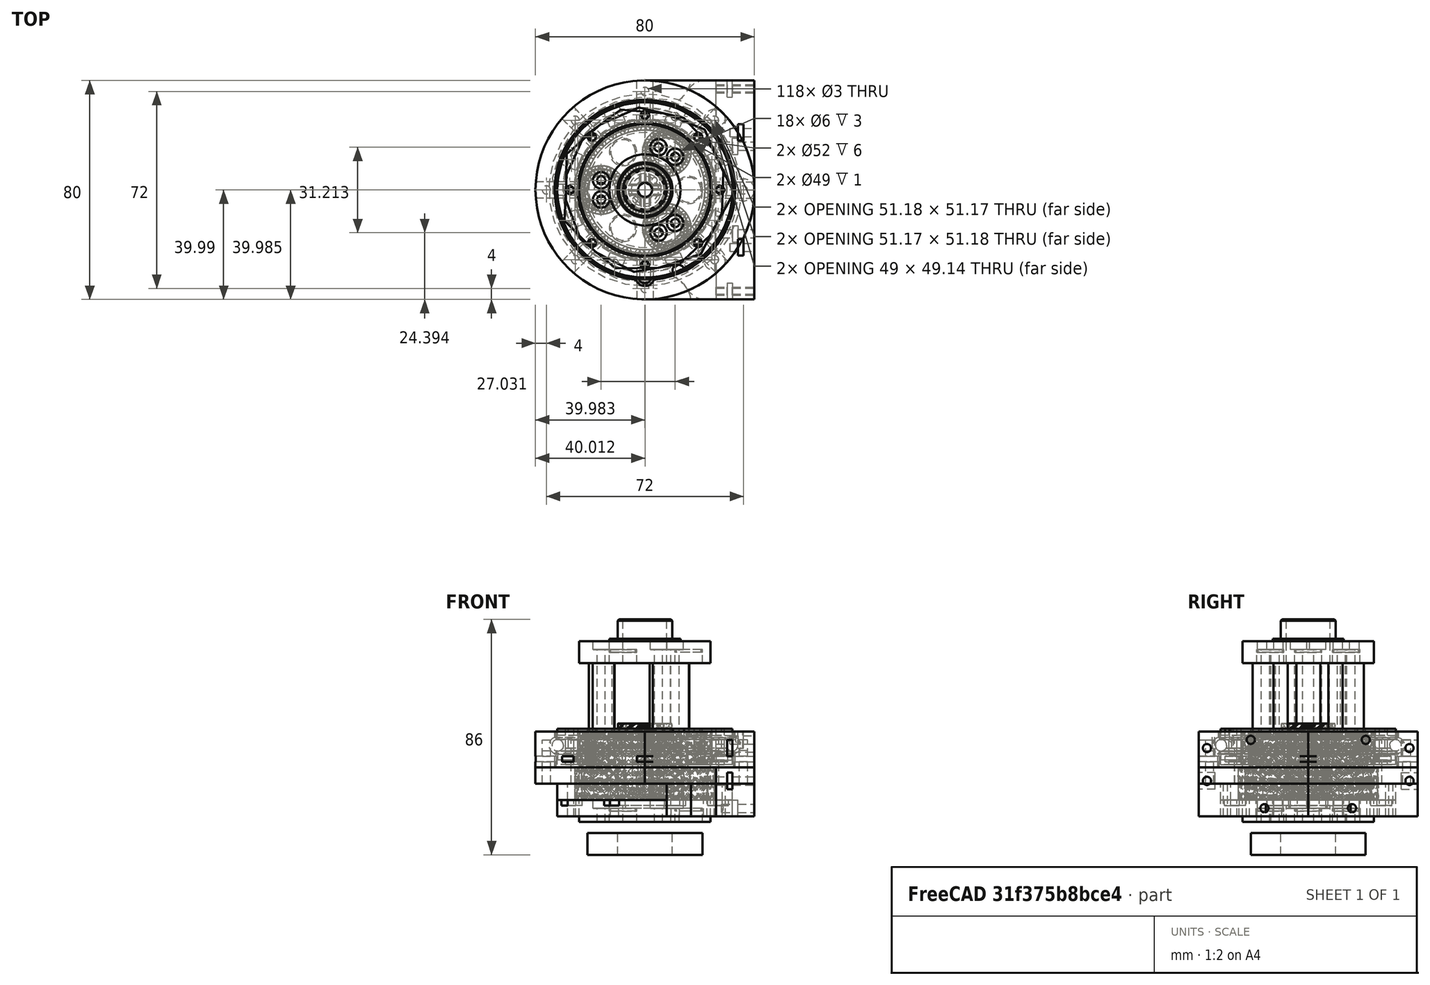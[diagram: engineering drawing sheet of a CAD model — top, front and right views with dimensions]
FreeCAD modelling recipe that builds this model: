
FCSTD DOCUMENT  (FreeCAD 0.19R24276 (Git))
Label: J-mini_024
License: All rights reserved
LicenseURL: http://en.wikipedia.org/wiki/All_rights_reserved
objects: Part::Cylinder×259, Part::Cut×154, Part::Box×112, Part::Compound×108, Part::FeaturePython×40, Mesh::Feature×18, Part::Chamfer×7, Part::Torus×6, Part::Mirroring×2, Part::Fillet×1
note: 689 computed .brp shape members not serialized (recipe doc carries the construction recipe); baked Part::Feature solids carry a one-line shape summary decoded from their .brp

FEATURE [Part::Cylinder] Cylinder190  label="Válec190"
  Angle = 360
  AttacherType = Attacher::AttachEngine3D
  Height = 20
  Placement = pos=(25.4558,-25.4558,0) rot=(0,0,-1;0.785398rad)
  Radius = 1.5
FEATURE [Part::Cylinder] Cylinder188  label="Válec188"
  Angle = 360
  AttacherType = Attacher::AttachEngine3D
  Height = 6
  Radius = 32
FEATURE [Part::Cylinder] Cylinder189  label="Válec189"
  Angle = 360
  AttacherType = Attacher::AttachEngine3D
  Height = 6
  Radius = 40
FEATURE [Part::Cylinder] Cylinder193  label="Válec193"
  Angle = 360
  AttacherType = Attacher::AttachEngine3D
  Height = 20
  Placement = pos=(25.4558,25.4558,0) rot=(0,0,1;0.785398rad)
  Radius = 1.5
FEATURE [Part::Cylinder] Cylinder196  label="Válec196"
  Angle = 360
  AttacherType = Attacher::AttachEngine3D
  Height = 20
  Placement = pos=(1.2e-14,-36,0) rot=(0,0,-1;1.5708rad)
  Radius = 1.5
FEATURE [Part::Cylinder] Cylinder194  label="Válec194"
  Angle = 360
  AttacherType = Attacher::AttachEngine3D
  Height = 20
  Placement = pos=(36,0,0) rot=(0,0,1;0rad)
  Radius = 1.5
FEATURE [Part::Cylinder] Cylinder191  label="Válec191"
  Angle = 360
  AttacherType = Attacher::AttachEngine3D
  Height = 20
  Placement = pos=(-25.4558,-25.4558,0) rot=(0,0,1;3.92699rad)
  Radius = 1.5
FEATURE [Part::Box] Box055  label="Krychle055"
  AttacherType = Attacher::AttachEngine3D
  Height = 2
  Length = 6
  Placement = pos=(22.8728,-12.7214,-2) rot=(0,0,-1;0.392699rad)
  Width = 6
FEATURE [Part::Cylinder] Cylinder198  label="Válec198"
  Angle = 360
  AttacherType = Attacher::AttachEngine3D
  Height = 20
  Placement = pos=(11.0978,-26.7925,-10) rot=(0,0,-1;1.1781rad)
  Radius = 1.5
FEATURE [Part::Box] Box057  label="Krychle057"
  AttacherType = Attacher::AttachEngine3D
  Height = 6
  Length = 2
  Placement = pos=(30,34,4) rot=(0,0,1;0rad)
  Width = 6
FEATURE [Part::Box] Box058  label="Krychle058"
  AttacherType = Attacher::AttachEngine3D
  Height = 2
  Length = 6
  Placement = pos=(12.7214,22.8728,-2) rot=(0,0,1;1.1781rad)
  Width = 6
FEATURE [Part::Box] Box059  label="Krychle059"
  AttacherType = Attacher::AttachEngine3D
  Height = 2
  Length = 6
  Placement = pos=(-25.1689,-7.17813,-2) rot=(0,0,1;3.53429rad)
  Width = 6
FEATURE [Part::Cylinder] Cylinder195  label="Válec195"
  Angle = 360
  AttacherType = Attacher::AttachEngine3D
  Height = 20
  Placement = pos=(-4e-15,36,0) rot=(0,0,1;1.5708rad)
  Radius = 1.5
FEATURE [Part::Box] Box056  label="Krychle056"
  AttacherType = Attacher::AttachEngine3D
  Height = 2
  Length = 6
  Placement = pos=(-7.17813,25.1689,-2) rot=(0,0,1;1.96349rad)
  Width = 6
FEATURE [Part::Cylinder] Cylinder197  label="Válec197"
  Angle = 360
  AttacherType = Attacher::AttachEngine3D
  Height = 20
  Placement = pos=(-36,-1.1e-14,0) rot=(0,0,1;3.14159rad)
  Radius = 1.5
FEATURE [Part::Cylinder] Cylinder199  label="Válec199"
  Angle = 360
  AttacherType = Attacher::AttachEngine3D
  Height = 20
  Placement = pos=(26.7925,11.0978,-10) rot=(0,0,1;0.392699rad)
  Radius = 1.5
FEATURE [Part::Box] Box060  label="Krychle060"
  AttacherType = Attacher::AttachEngine3D
  Height = 2
  Length = 6
  Placement = pos=(-22.8728,12.7214,-2) rot=(0,0,1;2.74889rad)
  Width = 6
FEATURE [Part::Box] Box061  label="Krychle061"
  AttacherType = Attacher::AttachEngine3D
  Height = 2
  Length = 6
  Placement = pos=(25.1689,7.17813,-2) rot=(0,0,1;0.392699rad)
  Width = 6
FEATURE [Part::Cylinder] Cylinder192  label="Válec192"
  Angle = 360
  AttacherType = Attacher::AttachEngine3D
  Height = 20
  Placement = pos=(-25.4558,25.4558,0) rot=(0,0,1;2.35619rad)
  Radius = 1.5
FEATURE [Part::FeaturePython] wormgear032  # WARN: FeaturePython — macro-defined, semantics opaque (R4)
  AttacherType = Attacher::AttachEngine3D
  Placement = pos=(0,0,0) rot=(0,0,1;0.011345rad)
  beta = 36.5317
  clearance = 0.25
  diameter = 49
  head = 0
  height = 20
  module = 1.1
  pressure_angle = 20
  reverse_pitch = true
  teeth = 33
  version = 0.0.3
FEATURE [Part::Cut] Cut142
  Base = -> Cylinder189
  Placement = pos=(0,0,6) rot=(0,0,-1;0.017453rad)
  Tool = -> wormgear032
FEATURE [Part::FeaturePython] wormgear033  # WARN: FeaturePython — macro-defined, semantics opaque (R4)
  AttacherType = Attacher::AttachEngine3D
  Placement = pos=(0,0,0) rot=(0,0,1;0.043633rad)
  beta = 36.5317
  clearance = 0.25
  diameter = 49
  head = 0
  height = 20
  module = 1.1
  pressure_angle = 20
  reverse_pitch = false
  teeth = 33
  version = 0.0.3
FEATURE [Part::Cut] Cut141
  Base = -> Cylinder188
  Tool = -> wormgear033
FEATURE [Part::FeaturePython] Tube010  # WARN: FeaturePython — macro-defined, semantics opaque (R4)
  AttacherType = Attacher::AttachEngine3D
  Height = 6
  InnerRadius = 26
  OuterRadius = 32
  Placement = pos=(0,0,-6) rot=(0,0,1;0rad)
FEATURE [Part::Compound] Compound127
  Links = -> [Cylinder190,Cylinder194,Cylinder193,Cylinder195,Cylinder192,Cylinder197,Cylinder191,Cylinder196]
FEATURE [Part::Cut] Cut144
  Base = -> Cut142
  Tool = -> Compound127
FEATURE [Part::Box] Box064  label="Krychle064"
  AttacherType = Attacher::AttachEngine3D
  Height = 6
  Length = 40
  Placement = pos=(0,0,6) rot=(0,0,1;0rad)
  Width = 40
FEATURE [Part::Cylinder] Cylinder205  label="Válec205"
  Angle = 360
  AttacherType = Attacher::AttachEngine3D
  Height = 20
  Placement = pos=(26.7925,-11.0978,-10) rot=(0,0,-1;0.392699rad)
  Radius = 1.5
FEATURE [Part::Cylinder] Cylinder204  label="Válec204"
  Angle = 360
  AttacherType = Attacher::AttachEngine3D
  Height = 20
  Placement = pos=(-26.7925,11.0978,-10) rot=(0,0,1;2.74889rad)
  Radius = 1.5
FEATURE [Part::Box] Box065  label="Krychle065"
  AttacherType = Attacher::AttachEngine3D
  Height = 6
  Length = 2
  Placement = pos=(30,34,4) rot=(0,0,1;0rad)
  Width = 6
FEATURE [Part::Cylinder] Cylinder209  label="Válec209"
  Angle = 360
  AttacherType = Attacher::AttachEngine3D
  Height = 20
  Placement = pos=(25.4558,25.4558,0) rot=(0,0,1;0.785398rad)
  Radius = 1.5
FEATURE [Part::Cylinder] Cylinder208  label="Válec208"
  Angle = 360
  AttacherType = Attacher::AttachEngine3D
  Height = 20
  Placement = pos=(36,0,0) rot=(0,0,1;0rad)
  Radius = 1.5
FEATURE [Part::Cylinder] Cylinder201  label="Válec201"
  Angle = 360
  AttacherType = Attacher::AttachEngine3D
  Height = 20
  Placement = pos=(-11.0978,26.7925,-10) rot=(0,0,1;1.96349rad)
  Radius = 1.5
FEATURE [Part::Box] Box066  label="Krychle066"
  AttacherType = Attacher::AttachEngine3D
  Height = 18
  Length = 14
  Placement = pos=(26,0,-6) rot=(0,0,1;0rad)
  Width = 40
FEATURE [Part::Cylinder] Cylinder200  label="Válec200"
  Angle = 360
  AttacherType = Attacher::AttachEngine3D
  Height = 20
  Placement = pos=(11.0978,26.7925,-10) rot=(0,0,1;1.1781rad)
  Radius = 1.5
FEATURE [Part::Cylinder] Cylinder210  label="Válec210"
  Angle = 360
  AttacherType = Attacher::AttachEngine3D
  Height = 30
  Placement = pos=(36,0,-24) rot=(0,0,1;0rad)
  Radius = 4
FEATURE [Part::Box] Box062  label="Krychle062"
  AttacherType = Attacher::AttachEngine3D
  Height = 2
  Length = 6
  Placement = pos=(-12.7214,-22.8728,-2) rot=(0,0,-1;1.96349rad)
  Width = 6
FEATURE [Part::Cylinder] Cylinder202  label="Válec202"
  Angle = 360
  AttacherType = Attacher::AttachEngine3D
  Height = 20
  Placement = pos=(-26.7925,-11.0978,-10) rot=(0,0,1;3.53429rad)
  Radius = 1.5
FEATURE [Part::Cylinder] Cylinder203  label="Válec203"
  Angle = 360
  AttacherType = Attacher::AttachEngine3D
  Height = 20
  Placement = pos=(-11.0978,-26.7925,-10) rot=(0,0,-1;1.96349rad)
  Radius = 1.5
FEATURE [Part::Compound] Compound125
  Links = -> [Cylinder199,Cylinder200,Cylinder201,Cylinder204,Cylinder202,Cylinder203,Cylinder198,Cylinder205]
FEATURE [Part::Box] Box063  label="Krychle063"
  AttacherType = Attacher::AttachEngine3D
  Height = 2
  Length = 6
  Placement = pos=(7.17813,-25.1689,-2) rot=(0,0,-1;1.1781rad)
  Width = 6
FEATURE [Part::Compound] Compound126
  Links = -> [Box061,Box058,Box056,Box060,Box059,Box062,Box063,Box055]
FEATURE [Part::Cylinder] Cylinder206  label="Válec206"
  Angle = 360
  AttacherType = Attacher::AttachEngine3D
  Height = 20
  Placement = pos=(26,37,7) rot=(0,1,0;1.5708rad)
  Radius = 1.5
FEATURE [Part::Cylinder] Cylinder207  label="Válec207"
  Angle = 360
  AttacherType = Attacher::AttachEngine3D
  Height = 6
  Placement = pos=(0,0,6) rot=(0,0,1;0rad)
  Radius = 40
FEATURE [Part::Cut] Cut138
  Base = -> Box064
  Tool = -> Cylinder207
FEATURE [Part::Cut] Cut135
  Base = -> Cut138
  Tool = -> Box057
FEATURE [Part::Cut] Cut134
  Base = -> Cut135
  Tool = -> Cylinder206
FEATURE [Part::Cut] Cut151
  Base = -> Tube010
  Tool = -> Compound126
FEATURE [Part::Cut] Cut136
  Base = -> Cut151
  Tool = -> Compound125
FEATURE [Part::Cylinder] Cylinder212  label="Válec212"
  Angle = 360
  AttacherType = Attacher::AttachEngine3D
  Height = 20
  Placement = pos=(26,37,7) rot=(0,1,0;1.5708rad)
  Radius = 1.5
FEATURE [Part::Cylinder] Cylinder220  label="Válec220"
  Angle = 360
  AttacherType = Attacher::AttachEngine3D
  Height = 30
  Placement = pos=(25.4558,25.4558,-24) rot=(0,0,1;0.785398rad)
  Radius = 4
FEATURE [Part::Cylinder] Cylinder214  label="Válec214"
  Angle = 360
  AttacherType = Attacher::AttachEngine3D
  Height = 20
  Placement = pos=(28,16,-3) rot=(0,1,0;1.5708rad)
  Radius = 1.5
FEATURE [Part::Compound] Compound132
  Links = -> [Cylinder214,Cylinder212]
FEATURE [Part::Cylinder] Cylinder217  label="Válec217"
  Angle = 360
  AttacherType = Attacher::AttachEngine3D
  Height = 12
  Placement = pos=(0,0,-6) rot=(0,0,1;0rad)
  Radius = 32
FEATURE [Part::Cylinder] Cylinder221  label="Válec221"
  Angle = 360
  AttacherType = Attacher::AttachEngine3D
  Height = 6
  Placement = pos=(0,0,6) rot=(0,0,1;0rad)
  Radius = 40
FEATURE [Part::Box] Box068  label="Krychle068"
  AttacherType = Attacher::AttachEngine3D
  Height = 6
  Length = 2
  Placement = pos=(30,34,4) rot=(0,0,1;0rad)
  Width = 6
FEATURE [Part::Box] Box070  label="Krychle070"
  AttacherType = Attacher::AttachEngine3D
  Height = 12
  Length = 18
  Placement = pos=(8,10,-6) rot=(0,0,1;0rad)
  Width = 30
FEATURE [Part::Box] Box071  label="Krychle071"
  AttacherType = Attacher::AttachEngine3D
  Height = 6
  Length = 40
  Placement = pos=(0,0,6) rot=(0,0,1;0rad)
  Width = 40
FEATURE [Part::Cut] Cut152
  Base = -> Box071
  Tool = -> Cylinder221
FEATURE [Part::Box] Box067  label="Krychle067"
  AttacherType = Attacher::AttachEngine3D
  Height = 6
  Length = 2
  Placement = pos=(32,13,-6) rot=(0,0,1;0rad)
  Width = 6
FEATURE [Part::Compound] Compound131
  Links = -> [Box067,Box065]
FEATURE [Part::Cylinder] Cylinder218  label="Válec218"
  Angle = 360
  AttacherType = Attacher::AttachEngine3D
  Height = 12
  Placement = pos=(0,0,-6) rot=(0,0,1;0rad)
  Radius = 32
FEATURE [Part::Cylinder] Cylinder219  label="Válec219"
  Angle = 360
  AttacherType = Attacher::AttachEngine3D
  Height = 12
  Placement = pos=(6,41.8,-6) rot=(0,0,1;0rad)
  Radius = 11
FEATURE [Part::Cut] Cut148
  Base = -> Box070
  Tool = -> Cylinder219
FEATURE [Part::Cut] Cut147
  Base = -> Cut148
  Tool = -> Cylinder218
FEATURE [Part::Cut] Cut149
  Base = -> Cut147
  Tool = -> Cylinder220
FEATURE [Part::Cylinder] Cylinder215  label="Válec215"
  Angle = 360
  AttacherType = Attacher::AttachEngine3D
  Height = 20
  Placement = pos=(26,37,7) rot=(0,1,0;1.5708rad)
  Radius = 1.5
FEATURE [Part::Box] Box069  label="Krychle069"
  AttacherType = Attacher::AttachEngine3D
  Height = 6
  Length = 2
  Placement = pos=(30,34,4) rot=(0,0,1;0rad)
  Width = 6
FEATURE [Part::Cut] Cut150
  Base = -> Cut152
  Tool = -> Box069
FEATURE [Part::Cut] Cut143
  Base = -> Cut150
  Tool = -> Cylinder215
FEATURE [Part::Cylinder] Cylinder213  label="Válec213"
  Angle = 360
  AttacherType = Attacher::AttachEngine3D
  Height = 30
  Placement = pos=(25.4558,25.4558,-24) rot=(0,0,1;0.785398rad)
  Radius = 4
FEATURE [Part::Cylinder] Cylinder216  label="Válec216"
  Angle = 360
  AttacherType = Attacher::AttachEngine3D
  Height = 20
  Placement = pos=(36,0,0) rot=(0,0,1;0rad)
  Radius = 1.5
FEATURE [Part::Cylinder] Cylinder211  label="Válec211"
  Angle = 360
  AttacherType = Attacher::AttachEngine3D
  Height = 12
  Placement = pos=(0,0,-6) rot=(0,0,1;0rad)
  Radius = 32
FEATURE [Part::Cut] Cut162
  Base = -> Box066
  Tool = -> Cylinder211
FEATURE [Part::Cut] Cut137
  Base = -> Cut162
  Tool = -> Cylinder210
FEATURE [Part::Cut] Cut140
  Base = -> Cut137
  Tool = -> Cylinder208
FEATURE [Part::Cut] Cut163
  Base = -> Cut140
  Tool = -> Cylinder213
FEATURE [Part::Cut] Cut146
  Base = -> Cut163
  Tool = -> Cylinder209
FEATURE [Part::Cut] Cut164
  Base = -> Cut146
  Tool = -> Compound132
FEATURE [Part::Cut] Cut145
  Base = -> Cut164
  Tool = -> Compound131
FEATURE [Part::Compound] Compound133
  Links = -> [Cut145,Cut149,Cut134]
FEATURE [Part::Cylinder] Cylinder223  label="Válec223"
  Angle = 360
  AttacherType = Attacher::AttachEngine3D
  Height = 30
  Placement = pos=(36,0,-24) rot=(0,0,1;0rad)
  Radius = 4
FEATURE [Part::Cylinder] Cylinder225  label="Válec225"
  Angle = 360
  AttacherType = Attacher::AttachEngine3D
  Height = 12
  Placement = pos=(0,0,-6) rot=(0,0,1;0rad)
  Radius = 32
FEATURE [Part::Cylinder] Cylinder222  label="Válec222"
  Angle = 360
  AttacherType = Attacher::AttachEngine3D
  Height = 20
  Placement = pos=(25.4558,25.4558,0) rot=(0,0,1;0.785398rad)
  Radius = 1.5
FEATURE [Part::Cylinder] Cylinder226  label="Válec226"
  Angle = 360
  AttacherType = Attacher::AttachEngine3D
  Height = 20
  Placement = pos=(26,37,7) rot=(0,1,0;1.5708rad)
  Radius = 1.5
FEATURE [Part::Cylinder] Cylinder227  label="Válec227"
  Angle = 360
  AttacherType = Attacher::AttachEngine3D
  Height = 12
  Placement = pos=(6,41.8,-6) rot=(0,0,1;0rad)
  Radius = 11
FEATURE [Part::Cylinder] Cylinder228  label="Válec228"
  Angle = 360
  AttacherType = Attacher::AttachEngine3D
  Height = 30
  Placement = pos=(25.4558,25.4558,-24) rot=(0,0,1;0.785398rad)
  Radius = 4
FEATURE [Part::Cylinder] Cylinder229  label="Válec229"
  Angle = 360
  AttacherType = Attacher::AttachEngine3D
  Height = 20
  Placement = pos=(28,16,-3) rot=(0,1,0;1.5708rad)
  Radius = 1.5
FEATURE [Part::Compound] Compound130
  Links = -> [Cylinder229,Cylinder226]
FEATURE [Part::Box] Box073  label="Krychle073"
  AttacherType = Attacher::AttachEngine3D
  Height = 12
  Length = 18
  Placement = pos=(8,10,-6) rot=(0,0,1;0rad)
  Width = 30
FEATURE [Part::Cut] Cut155
  Base = -> Box073
  Tool = -> Cylinder227
FEATURE [Part::Cut] Cut158
  Base = -> Cut155
  Tool = -> Cylinder225
FEATURE [Part::Cut] Cut156
  Base = -> Cut158
  Tool = -> Cylinder228
FEATURE [Part::Cylinder] Cylinder224  label="Válec224"
  Angle = 360
  AttacherType = Attacher::AttachEngine3D
  Height = 30
  Placement = pos=(25.4558,25.4558,-24) rot=(0,0,1;0.785398rad)
  Radius = 4
FEATURE [Part::Box] Box072  label="Krychle072"
  AttacherType = Attacher::AttachEngine3D
  Height = 18
  Length = 14
  Placement = pos=(26,0,-6) rot=(0,0,1;0rad)
  Width = 40
FEATURE [Part::Cut] Cut160
  Base = -> Box072
  Tool = -> Cylinder217
FEATURE [Part::Cut] Cut139
  Base = -> Cut160
  Tool = -> Cylinder223
FEATURE [Part::Cut] Cut161
  Base = -> Cut139
  Tool = -> Cylinder216
FEATURE [Part::Cut] Cut157
  Base = -> Cut161
  Tool = -> Cylinder224
FEATURE [Part::Cut] Cut153
  Base = -> Cut157
  Tool = -> Cylinder222
FEATURE [Part::Cut] Cut159
  Base = -> Cut153
  Tool = -> Compound130
FEATURE [Part::Box] Box074  label="Krychle074"
  AttacherType = Attacher::AttachEngine3D
  Height = 6
  Length = 2
  Placement = pos=(32,13,-6) rot=(0,0,1;0rad)
  Width = 6
FEATURE [Part::Compound] Compound128
  Links = -> [Box074,Box068]
FEATURE [Part::Cut] Cut154
  Base = -> Cut159
  Tool = -> Compound128
FEATURE [Part::Compound] Compound129
  Links = -> [Cut154,Cut156,Cut143]
FEATURE [Part::Mirroring] mirror001  label="Compound123 (mirrored)001"
  Base = (1,0,0)
  Normal = (1e-16,-1,0)
  Source = -> Compound129
FEATURE [Part::Compound] Compound134  label="jointovina_micro_monoblok_hrubo001"
  Links = -> [Compound133,mirror001,Cut136,Cut141,Cut144]
FEATURE [Part::Fillet] Fillet  label="J-mini_monoblock_old"
  Base = -> Compound134
  Edges = 2 edges r=8: [Edge90,Edge230]
FEATURE [Part::Torus] Torus006  label="Anuloid006"
  Angle1 = -180
  Angle2 = 180
  Angle3 = 360
  AttacherType = Attacher::AttachEngine3D
  Placement = pos=(0,0,20) rot=(0,0,1;0rad)
  Radius1 = 32
  Radius2 = 2.2
FEATURE [Part::Torus] Torus005  label="Anuloid005"
  Angle1 = -180
  Angle2 = 180
  Angle3 = 360
  AttacherType = Attacher::AttachEngine3D
  Placement = pos=(0,0,20) rot=(0,0,1;0rad)
  Radius1 = 32
  Radius2 = 2.2
FEATURE [Part::FeaturePython] wormgear043  # WARN: FeaturePython — macro-defined, semantics opaque (R4)
  AttacherType = Attacher::AttachEngine3D
  Placement = pos=(0,0,12) rot=(0,0,1;0.169297rad)
  beta = 35.3625
  clearance = 0.25
  diameter = 46.5
  head = 0.2
  height = 8
  module = 1.1
  pressure_angle = 20
  reverse_pitch = false
  teeth = 30
  version = 0.0.3
FEATURE [Part::FeaturePython] Tube051  # WARN: FeaturePython — macro-defined, semantics opaque (R4)
  AttacherType = Attacher::AttachEngine3D
  Height = 1
  InnerRadius = 24.5
  OuterRadius = 32
  Placement = pos=(0,0,25) rot=(0,0,1;0rad)
FEATURE [Part::FeaturePython] wormgear042  # WARN: FeaturePython — macro-defined, semantics opaque (R4)
  AttacherType = Attacher::AttachEngine3D
  Placement = pos=(0,0,18) rot=(0,0,-1;0.18326rad)
  beta = 35.3625
  clearance = 0.25
  diameter = 46.5
  head = 0.2
  height = 8
  module = 1.1
  pressure_angle = 20
  reverse_pitch = true
  teeth = 30
  version = 0.0.3
FEATURE [Part::Cylinder] Cylinder1256  label="Válec1256"
  Angle = 360
  AttacherType = Attacher::AttachEngine3D
  Height = 20
  Placement = pos=(1.1e-14,-27,19) rot=(0,0,1;3.14159rad)
  Radius = 1
FEATURE [Part::Box] Box403  label="Krychle403"
  AttacherType = Attacher::AttachEngine3D
  Height = 1.4
  Length = 4
  Placement = pos=(18.74,-15.91,23.6) rot=(0,0,1;3.92699rad)
  Width = 8
FEATURE [Part::Cylinder] Cylinder1250  label="Válec1250"
  Angle = 360
  AttacherType = Attacher::AttachEngine3D
  Height = 20
  Placement = pos=(-19.0919,19.0919,19) rot=(0,0,1;0.785398rad)
  Radius = 1
FEATURE [Part::Cylinder] Cylinder1254  label="Válec1254"
  Angle = 360
  AttacherType = Attacher::AttachEngine3D
  Height = 20
  Placement = pos=(-27,-4e-15,19) rot=(0,0,1;1.5708rad)
  Radius = 1
FEATURE [Part::Cylinder] Cylinder1253  label="Válec1253"
  Angle = 360
  AttacherType = Attacher::AttachEngine3D
  Height = 6
  Placement = pos=(0,0,13) rot=(0,0,1;0rad)
  Radius = 32
FEATURE [Part::Cut] Cut471
  Base = -> Cylinder1253
  Tool = -> wormgear043
FEATURE [Part::Cylinder] Cylinder1261  label="Válec1261"
  Angle = 360
  AttacherType = Attacher::AttachEngine3D
  Height = 20
  Placement = pos=(19.0919,-19.0919,19) rot=(0,0,1;3.92699rad)
  Radius = 1
FEATURE [Part::Cylinder] Cylinder1255  label="Válec1255"
  Angle = 360
  AttacherType = Attacher::AttachEngine3D
  Height = 20
  Placement = pos=(0,27,19) rot=(0,0,1;0rad)
  Radius = 1
FEATURE [Part::Box] Box404  label="Krychle404"
  AttacherType = Attacher::AttachEngine3D
  Height = 1.4
  Length = 4
  Placement = pos=(-15.91,-18.74,23.6) rot=(0,0,1;2.35619rad)
  Width = 8
FEATURE [Part::Cylinder] Cylinder1257  label="Válec1257"
  Angle = 360
  AttacherType = Attacher::AttachEngine3D
  Height = 20
  Placement = pos=(1.1e-14,-27,19) rot=(0,0,1;3.14159rad)
  Radius = 1
FEATURE [Part::Cylinder] Cylinder1266  label="Válec1266"
  Angle = 360
  AttacherType = Attacher::AttachEngine3D
  Height = 20
  Placement = pos=(-27,-4e-15,19) rot=(0,0,1;1.5708rad)
  Radius = 1
FEATURE [Part::Box] Box402  label="Krychle402"
  AttacherType = Attacher::AttachEngine3D
  Height = 1.4
  Length = 4
  Placement = pos=(-2,24.5,23.6) rot=(0,0,1;0rad)
  Width = 8
FEATURE [Part::Cylinder] Cylinder1252  label="Válec1252"
  Angle = 360
  AttacherType = Attacher::AttachEngine3D
  Height = 6
  Placement = pos=(0,0,19) rot=(0,0,1;0rad)
  Radius = 32
FEATURE [Part::Cut] Cut472
  Base = -> Cylinder1252
  Tool = -> wormgear042
FEATURE [Part::Cylinder] Cylinder1251  label="Válec1251"
  Angle = 360
  AttacherType = Attacher::AttachEngine3D
  Height = 20
  Placement = pos=(0,27,19) rot=(0,0,1;0rad)
  Radius = 1
FEATURE [Part::Box] Box406  label="Krychle406"
  AttacherType = Attacher::AttachEngine3D
  Height = 1.4
  Length = 4
  Placement = pos=(-24.5,-2,23.6) rot=(0,0,1;1.5708rad)
  Width = 8
FEATURE [Part::Cylinder] Cylinder1262  label="Válec1262"
  Angle = 360
  AttacherType = Attacher::AttachEngine3D
  Height = 10
  Placement = pos=(12.2459,-29.5641,20) rot=(0,0,1;0.392699rad)
  Radius = 2.2
FEATURE [Part::Cylinder] Cylinder1259  label="Válec1259"
  Angle = 360
  AttacherType = Attacher::AttachEngine3D
  Height = 20
  Placement = pos=(27,1e-14,19) rot=(0,0,-1;1.5708rad)
  Radius = 1
FEATURE [Part::Cylinder] Cylinder1260  label="Válec1260"
  Angle = 360
  AttacherType = Attacher::AttachEngine3D
  Height = 20
  Placement = pos=(19.0919,19.0919,19) rot=(0,0,-1;0.785398rad)
  Radius = 1
FEATURE [Part::Cylinder] Cylinder1258  label="Válec1258"
  Angle = 360
  AttacherType = Attacher::AttachEngine3D
  Height = 20
  Placement = pos=(-19.0919,-19.0919,19) rot=(0,0,1;2.35619rad)
  Radius = 1
FEATURE [Part::Compound] Compound681
  Links = -> [Cylinder1251,Cylinder1250,Cylinder1254,Cylinder1258,Cylinder1257,Cylinder1261,Cylinder1259,Cylinder1260]
FEATURE [Part::Box] Box408  label="Krychle408"
  AttacherType = Attacher::AttachEngine3D
  Height = 1.4
  Length = 4
  Placement = pos=(2,-24.5,23.6) rot=(0,0,1;3.14159rad)
  Width = 8
FEATURE [Part::Box] Box405  label="Krychle405"
  AttacherType = Attacher::AttachEngine3D
  Height = 1.4
  Length = 4
  Placement = pos=(-18.74,15.91,23.6) rot=(0,0,1;0.785398rad)
  Width = 8
FEATURE [Part::Box] Box409  label="Krychle409"
  AttacherType = Attacher::AttachEngine3D
  Height = 1.4
  Length = 4
  Placement = pos=(15.91,18.74,23.6) rot=(0,0,-1;0.785398rad)
  Width = 8
FEATURE [Part::Cylinder] Cylinder1263  label="Válec1263"
  Angle = 360
  AttacherType = Attacher::AttachEngine3D
  Height = 20
  Placement = pos=(-19.0919,19.0919,19) rot=(0,0,1;0.785398rad)
  Radius = 1
FEATURE [Part::Cylinder] Cylinder1264  label="Válec1264"
  Angle = 360
  AttacherType = Attacher::AttachEngine3D
  Height = 20
  Placement = pos=(-27,-4e-15,19) rot=(0,0,1;1.5708rad)
  Radius = 1
FEATURE [Part::Box] Box407  label="Krychle407"
  AttacherType = Attacher::AttachEngine3D
  Height = 1.4
  Length = 4
  Placement = pos=(24.5,2,23.6) rot=(0,0,-1;1.5708rad)
  Width = 8
FEATURE [Part::Compound] Compound678
  Links = -> [Box402,Box405,Box406,Box404,Box408,Box403,Box407,Box409]
FEATURE [Part::Cut] Cut474
  Base = -> Cut472
  Tool = -> Compound678
FEATURE [Part::Cut] Cut475
  Base = -> Cut474
  Tool = -> Compound681
FEATURE [Part::Cut] Cut478
  Base = -> Cut475
  Tool = -> Torus006
FEATURE [Part::Cut] Cut480
  Base = -> Cut478
  Tool = -> Cylinder1262
FEATURE [Part::Cylinder] Cylinder1265  label="Válec1265"
  Angle = 360
  AttacherType = Attacher::AttachEngine3D
  Height = 20
  Placement = pos=(-19.0919,-19.0919,19) rot=(0,0,1;2.35619rad)
  Radius = 1
FEATURE [Part::Cylinder] Cylinder1276  label="Válec1276"
  Angle = 360
  AttacherType = Attacher::AttachEngine3D
  Height = 20
  Placement = pos=(0,27,19) rot=(0,0,1;0rad)
  Radius = 1
FEATURE [Part::Cylinder] Cylinder1277  label="Válec1277"
  Angle = 360
  AttacherType = Attacher::AttachEngine3D
  Height = 20
  Placement = pos=(-19.0919,-19.0919,19) rot=(0,0,1;2.35619rad)
  Radius = 1
FEATURE [Part::Cylinder] Cylinder1272  label="Válec1272"
  Angle = 360
  AttacherType = Attacher::AttachEngine3D
  Height = 20
  Placement = pos=(-19.0919,19.0919,19) rot=(0,0,1;0.785398rad)
  Radius = 1
FEATURE [Part::Cylinder] Cylinder1271  label="Válec1271"
  Angle = 360
  AttacherType = Attacher::AttachEngine3D
  Height = 20
  Placement = pos=(27,1e-14,19) rot=(0,0,-1;1.5708rad)
  Radius = 1
FEATURE [Part::Cylinder] Cylinder1269  label="Válec1269"
  Angle = 360
  AttacherType = Attacher::AttachEngine3D
  Height = 20
  Placement = pos=(1.1e-14,-27,19) rot=(0,0,1;3.14159rad)
  Radius = 1
FEATURE [Part::Cylinder] Cylinder1274  label="Válec1274"
  Angle = 360
  AttacherType = Attacher::AttachEngine3D
  Height = 20
  Placement = pos=(27,1e-14,19) rot=(0,0,-1;1.5708rad)
  Radius = 1
FEATURE [Part::Cylinder] Cylinder1268  label="Válec1268"
  Angle = 360
  AttacherType = Attacher::AttachEngine3D
  Height = 20
  Placement = pos=(19.0919,-19.0919,19) rot=(0,0,1;3.92699rad)
  Radius = 1
FEATURE [Part::Cylinder] Cylinder1267  label="Válec1267"
  Angle = 360
  AttacherType = Attacher::AttachEngine3D
  Height = 15
  Placement = pos=(12.2459,-29.5641,20) rot=(0,0,1;0.392699rad)
  Radius = 2.2
FEATURE [Part::Cylinder] Cylinder1270  label="Válec1270"
  Angle = 360
  AttacherType = Attacher::AttachEngine3D
  Height = 20
  Placement = pos=(19.0919,19.0919,19) rot=(0,0,-1;0.785398rad)
  Radius = 1
FEATURE [Part::Cylinder] Cylinder1273  label="Válec1273"
  Angle = 360
  AttacherType = Attacher::AttachEngine3D
  Height = 20
  Placement = pos=(19.0919,19.0919,19) rot=(0,0,-1;0.785398rad)
  Radius = 1
FEATURE [Part::Compound] Compound679
  Links = -> [Cylinder1255,Cylinder1263,Cylinder1264,Cylinder1265,Cylinder1256,Cylinder1268,Cylinder1271,Cylinder1273]
FEATURE [Part::Cut] Cut473
  Base = -> Cut471
  Tool = -> Compound679
FEATURE [Part::Cut] Cut477
  Base = -> Cut473
  Tool = -> Torus005
FEATURE [Part::Compound] Compound680  label="jointovina_micro_rybovina002"
  Links = -> [Cut477,Cut480]
FEATURE [Part::Cylinder] Cylinder1275  label="Válec1275"
  Angle = 360
  AttacherType = Attacher::AttachEngine3D
  Height = 20
  Placement = pos=(19.0919,-19.0919,19) rot=(0,0,1;3.92699rad)
  Radius = 1
FEATURE [Part::Compound] Compound677
  Links = -> [Cylinder1276,Cylinder1272,Cylinder1266,Cylinder1277,Cylinder1269,Cylinder1275,Cylinder1274,Cylinder1270]
FEATURE [Part::Cut] Cut476
  Base = -> Tube051
  Tool = -> Compound677
FEATURE [Part::Cut] Cut479
  Base = -> Cut476
  Tool = -> Cylinder1267
FEATURE [Part::Compound] Compound682  label="J-mini_rybovina"
  Links = -> [Cut479,Compound680]
FEATURE [Part::FeaturePython] wormgear029  # WARN: FeaturePython — macro-defined, semantics opaque (R4)
  AttacherType = Attacher::AttachEngine3D
  Placement = pos=(-16,0,6) rot=(0,0,1;0.226893rad)
  beta = 40.4181
  clearance = 0.25
  diameter = 15.5
  head = 0
  height = 6
  module = 1.1
  pressure_angle = 20
  reverse_pitch = true
  teeth = 12
  version = 0.0.3
FEATURE [Part::FeaturePython] wormgear028  # WARN: FeaturePython — macro-defined, semantics opaque (R4)
  AttacherType = Attacher::AttachEngine3D
  Placement = pos=(-16,0,12) rot=(0,0,1;0.226893rad)
  beta = 36.8699
  clearance = 0.25
  diameter = 13.2
  head = 0
  height = 7
  module = 1.1
  pressure_angle = 20
  reverse_pitch = false
  teeth = 9
  version = 0.0.3
FEATURE [Part::FeaturePython] wormgear030  # WARN: FeaturePython — macro-defined, semantics opaque (R4)
  AttacherType = Attacher::AttachEngine3D
  Placement = pos=(-16,0,19) rot=(0,0,1;0.244346rad)
  beta = 36.8699
  clearance = 0.25
  diameter = 13.2
  head = 0
  height = 6
  module = 1.1
  pressure_angle = 20
  reverse_pitch = true
  teeth = 9
  version = 0.0.3
FEATURE [Part::FeaturePython] wormgear031  # WARN: FeaturePython — macro-defined, semantics opaque (R4)
  AttacherType = Attacher::AttachEngine3D
  Placement = pos=(-16,0,0) rot=(0,0,1;0.366519rad)
  beta = 40.4181
  clearance = 0.25
  diameter = 15.5
  head = 0
  height = 6
  module = 1.1
  pressure_angle = 20
  reverse_pitch = false
  teeth = 12
  version = 0.0.3
FEATURE [Part::Cylinder] Cylinder281  label="Válec281"
  Angle = 360
  AttacherType = Attacher::AttachEngine3D
  Height = 50
  Placement = pos=(-16,0,-10) rot=(0,0,1;0rad)
  Radius = 2.6
FEATURE [Part::Cut] Cut185
  Base = -> wormgear031
  Tool = -> Cylinder281
FEATURE [Part::Cylinder] Cylinder278  label="Válec278"
  Angle = 360
  AttacherType = Attacher::AttachEngine3D
  Height = 50
  Placement = pos=(-16,0,-10) rot=(0,0,1;0rad)
  Radius = 2.6
FEATURE [Part::Cut] Cut182
  Base = -> wormgear029
  Tool = -> Cylinder278
FEATURE [Part::Cylinder] Cylinder280  label="Válec280"
  Angle = 360
  AttacherType = Attacher::AttachEngine3D
  Height = 50
  Placement = pos=(-16,0,-10) rot=(0,0,1;0rad)
  Radius = 2.6
FEATURE [Part::Cut] Cut184
  Base = -> wormgear030
  Tool = -> Cylinder280
FEATURE [Part::Cylinder] Cylinder279  label="Válec279"
  Angle = 360
  AttacherType = Attacher::AttachEngine3D
  Height = 50
  Placement = pos=(-16,0,-10) rot=(0,0,1;0rad)
  Radius = 2.6
FEATURE [Part::Cut] Cut183
  Base = -> wormgear028
  Tool = -> Cylinder279
FEATURE [Part::Compound] Compound156  label="J-mini_outer-gear"
  Links = -> [Cut182,Cut183,Cut184,Cut185]
FEATURE [Part::Compound] Compound683  label="jointovina_micro_vnejskove001"
  Links = -> [Cut182,Cut183,Cut184,Cut185]
  Placement = pos=(0,0,0) rot=(0,0,1;2.0944rad)
FEATURE [Part::Compound] Compound684  label="jointovina_micro_vnejskove002"
  Links = -> [Cut182,Cut183,Cut184,Cut185]
  Placement = pos=(0,0,0) rot=(0,0,1;2.0944rad)
FEATURE [Part::Compound] Compound685  label="jointovina_micro_vnejskove003"
  Links = -> [Cut182,Cut183,Cut184,Cut185]
  Placement = pos=(0,0,0) rot=(0,0,1;4.18879rad)
FEATURE [Part::Compound] Compound686  label="jointovina_micro_vnejskove004"
  Links = -> [Cut182,Cut183,Cut184,Cut185]
  Placement = pos=(0,0,0) rot=(0,0,1;4.18879rad)
FEATURE [Part::Box] Box025  label="Krychle025"
  AttacherType = Attacher::AttachEngine3D
  Height = 10
  Length = 10
  Placement = pos=(-1.5,0,-1) rot=(0,0,-1;1.5708rad)
  Width = 3
FEATURE [Part::Cylinder] Cylinder041  label="Válec041"
  Angle = 360
  AttacherType = Attacher::AttachEngine3D
  Height = 6
  Placement = pos=(0,0,13) rot=(0,0,1;0rad)
  Radius = 7
FEATURE [Part::Box] Box024  label="Krychle024"
  AttacherType = Attacher::AttachEngine3D
  Height = 10
  Length = 10
  Placement = pos=(0,-1.5,-1) rot=(0,0,1;0rad)
  Width = 3
FEATURE [Part::Box] Box026  label="Krychle026"
  AttacherType = Attacher::AttachEngine3D
  Height = 10
  Length = 10
  Placement = pos=(0,1.5,-1) rot=(0,0,1;3.14159rad)
  Width = 3
FEATURE [Part::FeaturePython] Tube003  # WARN: FeaturePython — macro-defined, semantics opaque (R4)
  AttacherType = Attacher::AttachEngine3D
  Height = 10
  InnerRadius = 3.5
  OuterRadius = 7
  Placement = pos=(0,0,-1) rot=(0,0,1;0rad)
FEATURE [Part::Box] Box027  label="Krychle027"
  AttacherType = Attacher::AttachEngine3D
  Height = 10
  Length = 10
  Placement = pos=(1.5,0,-1) rot=(0,0,1;1.5708rad)
  Width = 3
FEATURE [Part::Compound] Compound020
  Links = -> [Box024,Box027,Box026,Box025]
FEATURE [Part::Cut] Cut003
  Base = -> Tube003
  Tool = -> Compound020
FEATURE [Part::Chamfer] Chamfer002
  Base = -> Cut003
  Edges = 8 edges r=0.5: [Edge5,Edge8,Edge20,Edge22,Edge29,Edge32,Edge44,Edge46]
  Placement = pos=(0,0,3) rot=(0,0,1;0rad)
FEATURE [Part::Cylinder] Cylinder042  label="Válec042"
  Angle = 360
  AttacherType = Attacher::AttachEngine3D
  Height = 13
  Placement = pos=(0,0,13) rot=(0,0,1;0rad)
  Radius = 2.6
FEATURE [Part::Cylinder] Cylinder044  label="Válec044"
  Angle = 360
  AttacherType = Attacher::AttachEngine3D
  Height = 12
  Placement = pos=(0,0,13) rot=(0,0,1;0rad)
  Radius = 2.6
FEATURE [Part::Cut] Cut005
  Base = -> Cylinder041
  Tool = -> Cylinder044
FEATURE [Part::Cylinder] Cylinder043  label="Válec043"
  Angle = 360
  AttacherType = Attacher::AttachEngine3D
  Height = 1
  Placement = pos=(0,0,12) rot=(0,0,1;0rad)
  Radius = 7
FEATURE [Part::FeaturePython] wormgear038  # WARN: FeaturePython — macro-defined, semantics opaque (R4)
  AttacherType = Attacher::AttachEngine3D
  Placement = pos=(0,0,19) rot=(0,0,1;0.453786rad)
  beta = 36.2538
  clearance = 0.25
  diameter = 18
  head = 0.2
  height = 6
  module = 1.1
  pressure_angle = 20
  reverse_pitch = false
  teeth = 12
  version = 0.0.3
FEATURE [Part::Cut] Cut004
  Base = -> wormgear038
  Tool = -> Cylinder042
FEATURE [Part::Compound] Compound021  label="J-mini_inner-gear_old"
  Links = -> [Chamfer002,Cut004,Cylinder043,Cut005]
FEATURE [Mesh::Feature] Mesh001  label="J-mini_outer-gear (Meshed)"
FEATURE [Part::Cylinder] Cylinder053  label="Válec053"
  Angle = 360
  AttacherType = Attacher::AttachEngine3D
  Height = 5
  Placement = pos=(0,0,5) rot=(0,0,1;0rad)
  Radius = 3
FEATURE [Part::Box] Box334  label="Krychle334"
  AttacherType = Attacher::AttachEngine3D
  Height = 10
  Length = 10
  Placement = pos=(0,0,0) rot=(0,0,1;1.5708rad)
  Width = 20
FEATURE [Part::Box] Box332  label="Krychle332"
  AttacherType = Attacher::AttachEngine3D
  Height = 10
  Length = 10
  Placement = pos=(0,0,0) rot=(0,0,-1;1.5708rad)
  Width = 20
FEATURE [Part::FeaturePython] wormgear039  # WARN: FeaturePython — macro-defined, semantics opaque (R4)
  AttacherType = Attacher::AttachEngine3D
  Placement = pos=(0,0,19) rot=(0,0,1;0.453786rad)
  beta = 36.2538
  clearance = 0.25
  diameter = 18
  head = 0.2
  height = 6
  module = 1.1
  pressure_angle = 20
  reverse_pitch = false
  teeth = 12
  version = 0.0.3
FEATURE [Part::Cylinder] Cylinder069  label="Válec069"
  Angle = 360
  AttacherType = Attacher::AttachEngine3D
  Height = 13
  Placement = pos=(0,0,13) rot=(0,0,1;0rad)
  Radius = 2.6
FEATURE [Part::Cut] Cut038
  Base = -> wormgear039
  Placement = pos=(0,0,-2) rot=(0,0,1;0rad)
  Tool = -> Cylinder069
FEATURE [Part::Cylinder] Cylinder067  label="Válec067"
  Angle = 360
  AttacherType = Attacher::AttachEngine3D
  Height = 12
  Placement = pos=(0,0,13) rot=(0,0,1;0rad)
  Radius = 2.6
FEATURE [Part::Cylinder] Cylinder068  label="Válec068"
  Angle = 360
  AttacherType = Attacher::AttachEngine3D
  Height = 6
  Placement = pos=(0,0,13) rot=(0,0,1;0rad)
  Radius = 7
FEATURE [Part::Cut] Cut036
  Base = -> Cylinder068
  Placement = pos=(0,0,-2) rot=(0,0,1;0rad)
  Tool = -> Cylinder067
FEATURE [Part::Cylinder] Cylinder059  label="Válec059"
  Angle = 360
  AttacherType = Attacher::AttachEngine3D
  Height = 20
  Placement = pos=(-3.5,-3.5,0) rot=(0,0,1;0rad)
  Radius = 1
FEATURE [Part::Cylinder] Cylinder063  label="Válec063"
  Angle = 360
  AttacherType = Attacher::AttachEngine3D
  Height = 20
  Placement = pos=(3.5,3.5,0) rot=(0,0,1;0rad)
  Radius = 1
FEATURE [Part::Cylinder] Cylinder064  label="Válec064"
  Angle = 360
  AttacherType = Attacher::AttachEngine3D
  Height = 20
  Placement = pos=(-3.5,-3.5,0) rot=(0,0,1;0rad)
  Radius = 1
FEATURE [Part::Cylinder] Cylinder060  label="Válec060"
  Angle = 360
  AttacherType = Attacher::AttachEngine3D
  Height = 20
  Placement = pos=(-3.5,-3.5,0) rot=(0,0,1;0rad)
  Radius = 1
FEATURE [Part::Cylinder] Cylinder065  label="Válec065"
  Angle = 360
  AttacherType = Attacher::AttachEngine3D
  Height = 20
  Placement = pos=(3.5,3.5,0) rot=(0,0,1;0rad)
  Radius = 1
FEATURE [Part::Cylinder] Cylinder061  label="Válec061"
  Angle = 360
  AttacherType = Attacher::AttachEngine3D
  Height = 20
  Placement = pos=(3.5,3.5,0) rot=(0,0,1;0rad)
  Radius = 1
FEATURE [Part::Cylinder] Cylinder055  label="Válec055"
  Angle = 360
  AttacherType = Attacher::AttachEngine3D
  Height = 5
  Placement = pos=(0,0,5) rot=(0,0,1;0rad)
  Radius = 3
FEATURE [Part::Cylinder] Cylinder066  label="Válec066"
  Angle = 360
  AttacherType = Attacher::AttachEngine3D
  Height = 1
  Placement = pos=(0,0,10) rot=(0,0,1;0rad)
  Radius = 7
FEATURE [Part::Cylinder] Cylinder058  label="Válec058"
  Angle = 360
  AttacherType = Attacher::AttachEngine3D
  Height = 2
  Placement = pos=(-3.5,-3.5,0) rot=(0,0,1;0rad)
  Radius = 2
FEATURE [Part::Cylinder] Cylinder056  label="Válec056"
  Angle = 360
  AttacherType = Attacher::AttachEngine3D
  Height = 20
  Placement = pos=(3.5,3.5,0) rot=(0,0,1;0rad)
  Radius = 1
FEATURE [Part::Cylinder] Cylinder057  label="Válec057"
  Angle = 360
  AttacherType = Attacher::AttachEngine3D
  Height = 2
  Placement = pos=(3.5,3.5,0) rot=(0,0,1;0rad)
  Radius = 2
FEATURE [Part::Cylinder] Cylinder054  label="Válec054"
  Angle = 360
  AttacherType = Attacher::AttachEngine3D
  Height = 5
  Radius = 3
FEATURE [Part::Cylinder] Cylinder062  label="Válec062"
  Angle = 360
  AttacherType = Attacher::AttachEngine3D
  Height = 20
  Placement = pos=(-3.5,-3.5,0) rot=(0,0,1;0rad)
  Radius = 1
FEATURE [Part::FeaturePython] Tube052  # WARN: FeaturePython — macro-defined, semantics opaque (R4)
  AttacherType = Attacher::AttachEngine3D
  Height = 10
  InnerRadius = 1
  OuterRadius = 7
FEATURE [Part::Compound] Compound030
  Links = -> [Box332,Box334]
FEATURE [Part::Cut] Cut030
  Base = -> Tube052
  Tool = -> Compound030
FEATURE [Part::Cut] Cut031
  Base = -> Cut030
  Tool = -> Cylinder054
FEATURE [Part::Cut] Cut032
  Base = -> Cut031
  Tool = -> Cylinder055
FEATURE [Part::Chamfer] Chamfer
  Base = -> Cylinder053
  Edges = 1 edges r=0.5: [Edge3]
FEATURE [Part::Compound] Compound031
  Links = -> [Cylinder057,Cylinder058]
FEATURE [Part::Cut] Cut033
  Base = -> Cut032
  Tool = -> Compound031
FEATURE [Part::Compound] Compound032
  Links = -> [Cylinder056,Cylinder059]
FEATURE [Part::Compound] Compound033
  Links = -> [Cylinder061,Cylinder060]
FEATURE [Part::Cut] Cut039
  Base = -> Cut038
  Tool = -> Compound033
FEATURE [Part::Cut] Cut034
  Base = -> Cut033
  Tool = -> Compound032
FEATURE [Part::Chamfer] Chamfer010
  Base = -> Cut034
  Edges = 4 edges r=0.5: [Edge9,Edge16,Edge32,Edge40]
FEATURE [Part::Compound] Compound034
  Links = -> [Cylinder063,Cylinder062]
FEATURE [Part::Cut] Cut037
  Base = -> Cut036
  Tool = -> Compound034
FEATURE [Part::Compound] Compound035
  Links = -> [Cylinder065,Cylinder064]
FEATURE [Part::Cut] Cut035
  Base = -> Cylinder066
  Tool = -> Compound035
FEATURE [Part::Compound] Compound036  label="J-mini_inner-gear_low"
  Links = -> [Cut037,Cut039,Cut035,Chamfer010,Chamfer]
  Placement = pos=(0,0,2) rot=(0,0,1;0rad)
FEATURE [Part::Cylinder] Cylinder850  label="Válec850"
  Angle = 360
  AttacherType = Attacher::AttachEngine3D
  Height = 5
  Placement = pos=(16,0,50) rot=(0,0,1;0rad)
  Radius = 5
FEATURE [Part::Cylinder] Cylinder860  label="Válec860"
  Angle = 360
  AttacherType = Attacher::AttachEngine3D
  Height = 60
  Placement = pos=(-3.5,16,0) rot=(0,0,1;0rad)
  Radius = 1.5
FEATURE [Part::Cylinder] Cylinder857  label="Válec857"
  Angle = 360
  AttacherType = Attacher::AttachEngine3D
  Height = 3
  Placement = pos=(3.5,16,55) rot=(0,0,1;0rad)
  Radius = 3
FEATURE [Part::Cylinder] Cylinder849  label="Válec849"
  Angle = 360
  AttacherType = Attacher::AttachEngine3D
  Height = 8
  Placement = pos=(0,0,50) rot=(0,0,1;0rad)
  Radius = 24
FEATURE [Part::Cylinder] Cylinder855  label="Válec855"
  Angle = 360
  AttacherType = Attacher::AttachEngine3D
  Height = 5
  Placement = pos=(-8,13.8564,50) rot=(0,0,1;2.0944rad)
  Radius = 5
FEATURE [Part::Cylinder] Cylinder851  label="Válec851"
  Angle = 360
  AttacherType = Attacher::AttachEngine3D
  Height = 16
  Placement = pos=(0,0,48) rot=(0,0,1;0rad)
  Radius = 8
FEATURE [Part::Cylinder] Cylinder856  label="Válec856"
  Angle = 360
  AttacherType = Attacher::AttachEngine3D
  Height = 5
  Placement = pos=(-8,-13.8564,50) rot=(0,0,1;4.18879rad)
  Radius = 5
FEATURE [Part::Cylinder] Cylinder858  label="Válec858"
  Angle = 360
  AttacherType = Attacher::AttachEngine3D
  Height = 3
  Placement = pos=(-3.5,16,55) rot=(0,0,1;0rad)
  Radius = 3
FEATURE [Part::Cylinder] Cylinder862  label="Válec862"
  Angle = 360
  AttacherType = Attacher::AttachEngine3D
  Height = 20
  Placement = pos=(-3.5,16,40) rot=(0,0,1;0rad)
  Radius = 1.5
FEATURE [Part::Box] Box335  label="Krychle335"
  AttacherType = Attacher::AttachEngine3D
  Height = 60
  Length = 60
  Placement = pos=(-30,-35,0) rot=(0,0,1;0rad)
  Width = 40
FEATURE [Part::Cylinder] Cylinder859  label="Válec859"
  Angle = 360
  AttacherType = Attacher::AttachEngine3D
  Height = 60
  Placement = pos=(3.5,16,0) rot=(0,0,1;0rad)
  Radius = 1.5
FEATURE [Part::Box] Box410  label="Krychle410"
  AttacherType = Attacher::AttachEngine3D
  Height = 60
  Length = 20
  Placement = pos=(-19.32,-5.18,0) rot=(0,0,1;0.383972rad)
  Width = 40
FEATURE [Part::Box] Box336  label="Krychle336"
  AttacherType = Attacher::AttachEngine3D
  Height = 60
  Length = 20
  Placement = pos=(0,0,0) rot=(0,0,-1;0.383972rad)
  Width = 40
FEATURE [Part::Cylinder] Cylinder861  label="Válec861"
  Angle = 360
  AttacherType = Attacher::AttachEngine3D
  Height = 20
  Placement = pos=(3.5,16,40) rot=(0,0,1;0rad)
  Radius = 1.5
FEATURE [Part::Compound] Compound572
  Links = -> [Cylinder861,Cylinder862]
  Placement = pos=(0,0,0) rot=(0,0,1;3.66519rad)
FEATURE [Part::Compound] Compound568
  Links = -> [Cylinder857,Cylinder858]
  Placement = pos=(0,0,0) rot=(0,0,1;3.66519rad)
FEATURE [Part::Compound] Compound559
  Links = -> [Cylinder856,Cylinder855,Cylinder850]
FEATURE [Part::Compound] Compound567
  Links = -> [Cylinder857,Cylinder858]
  Placement = pos=(0,0,0) rot=(0,0,-1;0.523599rad)
FEATURE [Part::FeaturePython] Tube036  # WARN: FeaturePython — macro-defined, semantics opaque (R4)
  AttacherType = Attacher::AttachEngine3D
  Height = 1
  InnerRadius = 4.5
  OuterRadius = 5
  Placement = pos=(-8,-13.8564,54) rot=(0,0,1;4.18879rad)
FEATURE [Part::FeaturePython] Tube032  # WARN: FeaturePython — macro-defined, semantics opaque (R4)
  AttacherType = Attacher::AttachEngine3D
  Height = 1
  InnerRadius = 4.5
  OuterRadius = 5
  Placement = pos=(16,0,54) rot=(0,0,1;0rad)
FEATURE [Part::FeaturePython] Tube035  # WARN: FeaturePython — macro-defined, semantics opaque (R4)
  AttacherType = Attacher::AttachEngine3D
  Height = 1
  InnerRadius = 4.5
  OuterRadius = 5
  Placement = pos=(-8,13.8564,54) rot=(0,0,1;2.0944rad)
FEATURE [Part::Compound] Compound575
  Links = -> [Tube035,Tube036,Tube032]
FEATURE [Part::FeaturePython] Tube037  # WARN: FeaturePython — macro-defined, semantics opaque (R4)
  AttacherType = Attacher::AttachEngine3D
  Height = 27
  InnerRadius = 12
  OuterRadius = 20.5
  Placement = pos=(0,0,23) rot=(0,0,1;0rad)
FEATURE [Part::Cut] Cut349
  Base = -> Cylinder849
  Tool = -> Cylinder851
FEATURE [Part::Cut] Cut354
  Base = -> Cut349
  Tool = -> Compound559
FEATURE [Part::Cut] Cut355
  Base = -> Tube037
  Tool = -> Box335
FEATURE [Part::Cut] Cut357
  Base = -> Cut355
  Tool = -> Box410
FEATURE [Part::Cut] Cut358
  Base = -> Cut357
  Tool = -> Box336
FEATURE [Part::Compound] Compound569
  Links = -> [Cylinder857,Cylinder858]
  Placement = pos=(0,0,0) rot=(0,0,1;1.5708rad)
FEATURE [Part::Compound] Compound570
  Links = -> [Compound567,Compound568,Compound569]
FEATURE [Part::Cut] Cut362
  Base = -> Cut354
  Tool = -> Compound570
FEATURE [Part::Compound] Compound571
  Links = -> [Cylinder861,Cylinder862]
  Placement = pos=(0,0,0) rot=(0,0,-1;0.523599rad)
FEATURE [Part::Compound] Compound573
  Links = -> [Cylinder861,Cylinder862]
  Placement = pos=(0,0,0) rot=(0,0,1;1.5708rad)
FEATURE [Part::Compound] Compound574
  Links = -> [Compound571,Compound572,Compound573]
FEATURE [Part::Cut] Cut363
  Base = -> Cut362
  Tool = -> Compound574
FEATURE [Part::Compound] Compound576  label="jointovina_micro_pikovina1"
  Links = -> [Compound575,Cut363]
FEATURE [Part::Compound] Compound565
  Links = -> [Cylinder859,Cylinder860]
FEATURE [Part::Cut] Cut468
  Base = -> Cut358
  Placement = pos=(0,0,0) rot=(0,0,-1;0.523599rad)
  Tool = -> Compound565
FEATURE [Part::Cut] Cut470
  Base = -> Cut358
  Placement = pos=(0,0,0) rot=(0,0,1;3.66519rad)
  Tool = -> Compound565
FEATURE [Part::Cut] Cut469
  Base = -> Cut358
  Placement = pos=(0,0,0) rot=(0,0,1;1.5708rad)
  Tool = -> Compound565
FEATURE [Part::Compound] Compound675  label="J-mini_pikovina"
  Links = -> [Compound576,Cut468,Cut469,Cut470]
FEATURE [Mesh::Feature] Mesh003  label="J-mini_pikovina (Meshed)"
FEATURE [Part::Box] Box411  label="Krychle411"
  AttacherType = Attacher::AttachEngine3D
  Height = 10
  Length = 10
  Placement = pos=(0,0,0) rot=(0,0,-1;1.5708rad)
  Width = 20
FEATURE [Part::Cylinder] Cylinder1278  label="Válec1278"
  Angle = 360
  AttacherType = Attacher::AttachEngine3D
  Height = 20
  Placement = pos=(-3.5,-3.5,0) rot=(0,0,1;0rad)
  Radius = 1
FEATURE [Part::Cylinder] Cylinder1279  label="Válec1279"
  Angle = 360
  AttacherType = Attacher::AttachEngine3D
  Height = 12
  Placement = pos=(0,0,13) rot=(0,0,1;0rad)
  Radius = 2.6
FEATURE [Part::Cylinder] Cylinder1280  label="Válec1280"
  Angle = 360
  AttacherType = Attacher::AttachEngine3D
  Height = 20
  Placement = pos=(3.5,3.5,0) rot=(0,0,1;0rad)
  Radius = 1
FEATURE [Part::Cylinder] Cylinder1281  label="Válec1281"
  Angle = 360
  AttacherType = Attacher::AttachEngine3D
  Height = 20
  Placement = pos=(3.5,3.5,0) rot=(0,0,1;0rad)
  Radius = 1
FEATURE [Part::Cylinder] Cylinder1282  label="Válec1282"
  Angle = 360
  AttacherType = Attacher::AttachEngine3D
  Height = 13
  Placement = pos=(0,0,13) rot=(0,0,1;0rad)
  Radius = 2.6
FEATURE [Part::Cylinder] Cylinder1283  label="Válec1283"
  Angle = 360
  AttacherType = Attacher::AttachEngine3D
  Height = 20
  Placement = pos=(-3.5,-3.5,0) rot=(0,0,1;0rad)
  Radius = 1
FEATURE [Part::Compound] Compound693
  Links = -> [Cylinder1280,Cylinder1283]
FEATURE [Part::Cylinder] Cylinder1284  label="Válec1284"
  Angle = 360
  AttacherType = Attacher::AttachEngine3D
  Height = 1
  Placement = pos=(0,0,10) rot=(0,0,1;0rad)
  Radius = 7
FEATURE [Part::Cylinder] Cylinder1285  label="Válec1285"
  Angle = 360
  AttacherType = Attacher::AttachEngine3D
  Height = 20
  Placement = pos=(-3.5,-3.5,0) rot=(0,0,1;0rad)
  Radius = 1
FEATURE [Part::Cylinder] Cylinder1286  label="Válec1286"
  Angle = 360
  AttacherType = Attacher::AttachEngine3D
  Height = 5
  Radius = 3
FEATURE [Part::Cylinder] Cylinder1287  label="Válec1287"
  Angle = 360
  AttacherType = Attacher::AttachEngine3D
  Height = 2
  Placement = pos=(-3.5,-3.5,0) rot=(0,0,1;0rad)
  Radius = 2
FEATURE [Part::Cylinder] Cylinder1288  label="Válec1288"
  Angle = 360
  AttacherType = Attacher::AttachEngine3D
  Height = 2
  Placement = pos=(3.5,3.5,0) rot=(0,0,1;0rad)
  Radius = 2
FEATURE [Part::Compound] Compound691
  Links = -> [Cylinder1288,Cylinder1287]
FEATURE [Part::Box] Box412  label="Krychle412"
  AttacherType = Attacher::AttachEngine3D
  Height = 10
  Length = 10
  Placement = pos=(0,0,0) rot=(0,0,1;1.5708rad)
  Width = 20
FEATURE [Part::Compound] Compound690
  Links = -> [Box411,Box412]
FEATURE [Part::Cylinder] Cylinder1289  label="Válec1289"
  Angle = 360
  AttacherType = Attacher::AttachEngine3D
  Height = 5
  Placement = pos=(0,0,5) rot=(0,0,1;0rad)
  Radius = 3
FEATURE [Part::Cylinder] Cylinder1290  label="Válec1290"
  Angle = 360
  AttacherType = Attacher::AttachEngine3D
  Height = 5
  Placement = pos=(0,0,5) rot=(0,0,1;0rad)
  Radius = 3
FEATURE [Part::Chamfer] Chamfer012
  Base = -> Cylinder1290
  Edges = 1 edges r=0.5: [Edge3]
FEATURE [Part::Cylinder] Cylinder1291  label="Válec1291"
  Angle = 360
  AttacherType = Attacher::AttachEngine3D
  Height = 20
  Placement = pos=(3.5,3.5,0) rot=(0,0,1;0rad)
  Radius = 1
FEATURE [Part::Compound] Compound692
  Links = -> [Cylinder1291,Cylinder1278]
FEATURE [Part::Cylinder] Cylinder1292  label="Válec1292"
  Angle = 360
  AttacherType = Attacher::AttachEngine3D
  Height = 20
  Placement = pos=(-3.5,-3.5,0) rot=(0,0,1;0rad)
  Radius = 1
FEATURE [Part::Compound] Compound687
  Links = -> [Cylinder1281,Cylinder1292]
FEATURE [Part::Cylinder] Cylinder1293  label="Válec1293"
  Angle = 360
  AttacherType = Attacher::AttachEngine3D
  Height = 9
  Placement = pos=(0,0,13) rot=(0,0,1;0rad)
  Radius = 7
FEATURE [Part::Cylinder] Cylinder1294  label="Válec1294"
  Angle = 360
  AttacherType = Attacher::AttachEngine3D
  Height = 20
  Placement = pos=(3.5,3.5,0) rot=(0,0,1;0rad)
  Radius = 1
FEATURE [Part::Compound] Compound688
  Links = -> [Cylinder1294,Cylinder1285]
FEATURE [Part::FeaturePython] Tube053  # WARN: FeaturePython — macro-defined, semantics opaque (R4)
  AttacherType = Attacher::AttachEngine3D
  Height = 10
  InnerRadius = 1
  OuterRadius = 7
FEATURE [Part::FeaturePython] wormgear044  # WARN: FeaturePython — macro-defined, semantics opaque (R4)
  AttacherType = Attacher::AttachEngine3D
  Placement = pos=(0,0,19) rot=(0,0,1;0.453786rad)
  beta = 37.8283
  clearance = 0.25
  diameter = 17
  head = 0.2
  height = 6
  module = 1.1
  pressure_angle = 20
  reverse_pitch = false
  teeth = 12
  version = 0.0.3
FEATURE [Part::Cut] Cut487
  Base = -> Tube053
  Tool = -> Compound690
FEATURE [Part::Cut] Cut485
  Base = -> Cut487
  Tool = -> Cylinder1286
FEATURE [Part::Cut] Cut482
  Base = -> Cut485
  Tool = -> Cylinder1289
FEATURE [Part::Cut] Cut486
  Base = -> Cut482
  Tool = -> Compound691
FEATURE [Part::Cut] Cut481
  Base = -> Cut486
  Tool = -> Compound687
FEATURE [Part::Chamfer] Chamfer011
  Base = -> Cut481
  Edges = 4 edges r=0.5: [Edge9,Edge16,Edge32,Edge40]
FEATURE [Part::Cut] Cut488
  Base = -> Cylinder1284
  Tool = -> Compound692
FEATURE [Part::Cut] Cut489
  Base = -> wormgear044
  Placement = pos=(0,0,-2) rot=(0,0,1;0rad)
  Tool = -> Cylinder1282
FEATURE [Part::Cut] Cut483
  Base = -> Cut489
  Placement = pos=(0,0,3) rot=(0,0,1;0rad)
  Tool = -> Compound688
FEATURE [Part::Cut] Cut490
  Base = -> Cylinder1293
  Placement = pos=(0,0,-2) rot=(0,0,1;0rad)
  Tool = -> Cylinder1279
FEATURE [Part::Cut] Cut484
  Base = -> Cut490
  Tool = -> Compound693
FEATURE [Part::Compound] Compound689  label="J-mini_inner-gear-high"
  Links = -> [Cut484,Cut483,Cut488,Chamfer011,Chamfer012]
  Placement = pos=(0,0,2) rot=(0,0,1;0rad)
FEATURE [Mesh::Feature] Mesh004  label="J-mini_inner-gear-high (Meshed)"
FEATURE [Part::Cylinder] Cylinder1295  label="Válec1295"
  Angle = 360
  AttacherType = Attacher::AttachEngine3D
  Height = 20
  Placement = pos=(0,27.5,10) rot=(0,0,1;0rad)
  Radius = 1.5
FEATURE [Part::Cylinder] Cylinder1296  label="Válec1296"
  Angle = 360
  AttacherType = Attacher::AttachEngine3D
  Height = 20
  Placement = pos=(-19.4454,-19.4454,10) rot=(0,0,1;2.35619rad)
  Radius = 1.5
FEATURE [Part::Cylinder] Cylinder1297  label="Válec1297"
  Angle = 360
  AttacherType = Attacher::AttachEngine3D
  Height = 20
  Placement = pos=(19.4454,19.4454,10) rot=(0,0,-1;0.785398rad)
  Radius = 1.5
FEATURE [Part::Cylinder] Cylinder1298  label="Válec1298"
  Angle = 360
  AttacherType = Attacher::AttachEngine3D
  Height = 20
  Placement = pos=(1.1e-14,-27.5,10) rot=(0,0,1;3.14159rad)
  Radius = 1.5
FEATURE [Part::Cylinder] Cylinder1299  label="Válec1299"
  Angle = 360
  AttacherType = Attacher::AttachEngine3D
  Height = 20
  Placement = pos=(19.4454,-19.4454,10) rot=(0,0,1;3.92699rad)
  Radius = 1.5
FEATURE [Part::Cylinder] Cylinder1300  label="Válec1300"
  Angle = 360
  AttacherType = Attacher::AttachEngine3D
  Height = 20
  Placement = pos=(-27.5,-4e-15,10) rot=(0,0,1;1.5708rad)
  Radius = 1.5
FEATURE [Part::Cylinder] Cylinder1301  label="Válec1301"
  Angle = 360
  AttacherType = Attacher::AttachEngine3D
  Height = 20
  Placement = pos=(-19.4454,19.4454,10) rot=(0,0,1;0.785398rad)
  Radius = 1.5
FEATURE [Part::Cylinder] Cylinder1302  label="Válec1302"
  Angle = 360
  AttacherType = Attacher::AttachEngine3D
  Height = 20
  Placement = pos=(27.5,1.2e-14,10) rot=(0,0,-1;1.5708rad)
  Radius = 1.5
FEATURE [Part::Cylinder] Cylinder1303  label="Válec1303"
  Angle = 360
  AttacherType = Attacher::AttachEngine3D
  Height = 6
  Placement = pos=(0,0,13) rot=(0,0,1;0rad)
  Radius = 32
FEATURE [Part::Cylinder] Cylinder1304  label="Válec1304"
  Angle = 360
  AttacherType = Attacher::AttachEngine3D
  Height = 10
  Placement = pos=(12.2459,-29.5641,20) rot=(0,0,1;0.392699rad)
  Radius = 2.2
FEATURE [Part::Cylinder] Cylinder1305  label="Válec1305"
  Angle = 360
  AttacherType = Attacher::AttachEngine3D
  Height = 6
  Placement = pos=(0,0,19) rot=(0,0,1;0rad)
  Radius = 32
FEATURE [Part::Cylinder] Cylinder1306  label="Válec1306"
  Angle = 360
  AttacherType = Attacher::AttachEngine3D
  Height = 15
  Placement = pos=(12.2459,-29.5641,20) rot=(0,0,1;0.392699rad)
  Radius = 2.2
FEATURE [Part::Cylinder] Cylinder1307  label="Válec1307"
  Angle = 360
  AttacherType = Attacher::AttachEngine3D
  Height = 20
  Placement = pos=(27.5,1.2e-14,10) rot=(0,0,-1;1.5708rad)
  Radius = 1.5
FEATURE [Part::Cylinder] Cylinder1308  label="Válec1308"
  Angle = 360
  AttacherType = Attacher::AttachEngine3D
  Height = 20
  Placement = pos=(0,27.5,10) rot=(0,0,1;0rad)
  Radius = 1.5
FEATURE [Part::Cylinder] Cylinder1309  label="Válec1309"
  Angle = 360
  AttacherType = Attacher::AttachEngine3D
  Height = 20
  Placement = pos=(19.4454,19.4454,10) rot=(0,0,-1;0.785398rad)
  Radius = 1.5
FEATURE [Part::Cylinder] Cylinder1310  label="Válec1310"
  Angle = 360
  AttacherType = Attacher::AttachEngine3D
  Height = 20
  Placement = pos=(-19.4454,-19.4454,10) rot=(0,0,1;2.35619rad)
  Radius = 1.5
FEATURE [Part::Cylinder] Cylinder1311  label="Válec1311"
  Angle = 360
  AttacherType = Attacher::AttachEngine3D
  Height = 20
  Placement = pos=(19.4454,-19.4454,10) rot=(0,0,1;3.92699rad)
  Radius = 1.5
FEATURE [Part::Cylinder] Cylinder1312  label="Válec1312"
  Angle = 360
  AttacherType = Attacher::AttachEngine3D
  Height = 20
  Placement = pos=(0,27.5,10) rot=(0,0,1;0rad)
  Radius = 1.5
FEATURE [Part::Cylinder] Cylinder1313  label="Válec1313"
  Angle = 360
  AttacherType = Attacher::AttachEngine3D
  Height = 20
  Placement = pos=(-27.5,-4e-15,10) rot=(0,0,1;1.5708rad)
  Radius = 1.5
FEATURE [Part::Cylinder] Cylinder1314  label="Válec1314"
  Angle = 360
  AttacherType = Attacher::AttachEngine3D
  Height = 20
  Placement = pos=(-19.4454,19.4454,10) rot=(0,0,1;0.785398rad)
  Radius = 1.5
FEATURE [Part::Cylinder] Cylinder1315  label="Válec1315"
  Angle = 360
  AttacherType = Attacher::AttachEngine3D
  Height = 20
  Placement = pos=(1.1e-14,-27.5,10) rot=(0,0,1;3.14159rad)
  Radius = 1.5
FEATURE [Part::Torus] Torus008  label="Anuloid008"
  Angle1 = -180
  Angle2 = 180
  Angle3 = 360
  AttacherType = Attacher::AttachEngine3D
  Placement = pos=(0,0,20) rot=(0,0,1;0rad)
  Radius1 = 32
  Radius2 = 2.2
FEATURE [Part::Torus] Torus007  label="Anuloid007"
  Angle1 = -180
  Angle2 = 180
  Angle3 = 360
  AttacherType = Attacher::AttachEngine3D
  Placement = pos=(0,0,20) rot=(0,0,1;0rad)
  Radius1 = 32
  Radius2 = 2.2
FEATURE [Part::Compound] Compound
  Links = -> [Cylinder1295,Cylinder1301,Cylinder1300,Cylinder1296,Cylinder1298,Cylinder1302,Cylinder1299,Cylinder1297]
FEATURE [Part::Box] Box424  label="Krychle424"
  AttacherType = Attacher::AttachEngine3D
  Height = 2
  Length = 6
  Placement = pos=(3,-24.5,23.6) rot=(0,0,1;3.14159rad)
  Width = 8
FEATURE [Part::Cylinder] Cylinder1316  label="Válec1316"
  Angle = 360
  AttacherType = Attacher::AttachEngine3D
  Height = 20
  Placement = pos=(27.5,1.2e-14,10) rot=(0,0,-1;1.5708rad)
  Radius = 1.5
FEATURE [Part::Box] Box427  label="Krychle427"
  AttacherType = Attacher::AttachEngine3D
  Height = 2
  Length = 6
  Placement = pos=(-19.4454,15.2028,23.6) rot=(0,0,1;0.785398rad)
  Width = 8
FEATURE [Part::Cylinder] Cylinder1317  label="Válec1317"
  Angle = 360
  AttacherType = Attacher::AttachEngine3D
  Height = 20
  Placement = pos=(1.1e-14,-27.5,10) rot=(0,0,1;3.14159rad)
  Radius = 1.5
FEATURE [Part::Cylinder] Cylinder1318  label="Válec1318"
  Angle = 360
  AttacherType = Attacher::AttachEngine3D
  Height = 20
  Placement = pos=(-19.4454,-19.4454,10) rot=(0,0,1;2.35619rad)
  Radius = 1.5
FEATURE [Part::Cylinder] Cylinder1319  label="Válec1319"
  Angle = 360
  AttacherType = Attacher::AttachEngine3D
  Height = 20
  Placement = pos=(-27.5,-4e-15,10) rot=(0,0,1;1.5708rad)
  Radius = 1.5
FEATURE [Part::Cylinder] Cylinder1320  label="Válec1320"
  Angle = 360
  AttacherType = Attacher::AttachEngine3D
  Height = 20
  Placement = pos=(19.4454,-19.4454,10) rot=(0,0,1;3.92699rad)
  Radius = 1.5
FEATURE [Part::Box] Box418  label="Krychle418"
  AttacherType = Attacher::AttachEngine3D
  Height = 2
  Length = 6
  Placement = pos=(-3,24.5,23.6) rot=(0,0,1;0rad)
  Width = 8
FEATURE [Part::Cylinder] Cylinder1321  label="Válec1321"
  Angle = 360
  AttacherType = Attacher::AttachEngine3D
  Height = 20
  Placement = pos=(-19.4454,19.4454,10) rot=(0,0,1;0.785398rad)
  Radius = 1.5
FEATURE [Part::Cylinder] Cylinder1322  label="Válec1322"
  Angle = 360
  AttacherType = Attacher::AttachEngine3D
  Height = 20
  Placement = pos=(19.4454,19.4454,10) rot=(0,0,-1;0.785398rad)
  Radius = 1.5
FEATURE [Part::Box] Box419  label="Krychle419"
  AttacherType = Attacher::AttachEngine3D
  Height = 2
  Length = 6
  Placement = pos=(-19.4454,15.2028,23.6) rot=(0,0,1;0.785398rad)
  Width = 8
FEATURE [Part::Box] Box421  label="Krychle421"
  AttacherType = Attacher::AttachEngine3D
  Height = 2
  Length = 6
  Placement = pos=(19.4454,-15.2028,23.6) rot=(0,0,1;3.92699rad)
  Width = 8
FEATURE [Part::Box] Box422  label="Krychle422"
  AttacherType = Attacher::AttachEngine3D
  Height = 2
  Length = 6
  Placement = pos=(24.5,3,23.6) rot=(0,0,-1;1.5708rad)
  Width = 8
FEATURE [Part::Box] Box423  label="Krychle423"
  AttacherType = Attacher::AttachEngine3D
  Height = 2
  Length = 6
  Placement = pos=(15.2028,19.4454,23.6) rot=(0,0,-1;0.785398rad)
  Width = 8
FEATURE [Part::Box] Box420  label="Krychle420"
  AttacherType = Attacher::AttachEngine3D
  Height = 2
  Length = 6
  Placement = pos=(-15.2028,-19.4454,23.6) rot=(0,0,1;2.35619rad)
  Width = 8
FEATURE [Part::Box] Box425  label="Krychle425"
  AttacherType = Attacher::AttachEngine3D
  Height = 2
  Length = 6
  Placement = pos=(-24.5,-3,23.6) rot=(0,0,1;1.5708rad)
  Width = 8
FEATURE [Part::Box] Box426  label="Krychle426"
  AttacherType = Attacher::AttachEngine3D
  Height = 2
  Length = 6
  Placement = pos=(-3,24.5,23.6) rot=(0,0,1;0rad)
  Width = 8
FEATURE [Part::Box] Box428  label="Krychle428"
  AttacherType = Attacher::AttachEngine3D
  Height = 2
  Length = 6
  Placement = pos=(-15.2028,-19.4454,23.6) rot=(0,0,1;2.35619rad)
  Width = 8
FEATURE [Part::Box] Box429  label="Krychle429"
  AttacherType = Attacher::AttachEngine3D
  Height = 2
  Length = 6
  Placement = pos=(19.4454,-15.2028,23.6) rot=(0,0,1;3.92699rad)
  Width = 8
FEATURE [Part::Box] Box431  label="Krychle431"
  AttacherType = Attacher::AttachEngine3D
  Height = 2
  Length = 6
  Placement = pos=(15.2028,19.4454,23.6) rot=(0,0,-1;0.785398rad)
  Width = 8
FEATURE [Part::Box] Box432  label="Krychle432"
  AttacherType = Attacher::AttachEngine3D
  Height = 2
  Length = 6
  Placement = pos=(3,-24.5,23.6) rot=(0,0,1;3.14159rad)
  Width = 8
FEATURE [Part::Box] Box433  label="Krychle433"
  AttacherType = Attacher::AttachEngine3D
  Height = 2
  Length = 6
  Placement = pos=(-24.5,-3,23.6) rot=(0,0,1;1.5708rad)
  Width = 8
FEATURE [Part::Box] Box430  label="Krychle430"
  AttacherType = Attacher::AttachEngine3D
  Height = 2
  Length = 6
  Placement = pos=(24.5,3,23.6) rot=(0,0,-1;1.5708rad)
  Width = 8
FEATURE [Part::FeaturePython] wormgear045  # WARN: FeaturePython — macro-defined, semantics opaque (R4)
  AttacherType = Attacher::AttachEngine3D
  Placement = pos=(0,0,18) rot=(0,0,-1;0.18326rad)
  beta = 35.3625
  clearance = 0.25
  diameter = 46.5
  head = 0.2
  height = 8
  module = 1.1
  pressure_angle = 20
  reverse_pitch = true
  teeth = 30
  version = 0.0.3
FEATURE [Part::FeaturePython] Tube054  # WARN: FeaturePython — macro-defined, semantics opaque (R4)
  AttacherType = Attacher::AttachEngine3D
  Height = 1
  InnerRadius = 24.5
  OuterRadius = 32
  Placement = pos=(0,0,25) rot=(0,0,1;0rad)
FEATURE [Part::FeaturePython] wormgear046  # WARN: FeaturePython — macro-defined, semantics opaque (R4)
  AttacherType = Attacher::AttachEngine3D
  Placement = pos=(0,0,12) rot=(0,0,1;0.169297rad)
  beta = 35.3625
  clearance = 0.25
  diameter = 46.5
  head = 0.2
  height = 8
  module = 1.1
  pressure_angle = 20
  reverse_pitch = false
  teeth = 30
  version = 0.0.3
FEATURE [Part::Cut] Cut494
  Base = -> Cylinder1303
  Tool = -> wormgear046
FEATURE [Part::Cut] Cut491
  Base = -> Cut494
  Tool = -> Torus008
FEATURE [Part::Cut] Cut497
  Base = -> Tube054
  Tool = -> Cylinder1306
FEATURE [Part::Cut] Cut492
  Base = -> Cut497
  Tool = -> Compound
FEATURE [Part::Cut] Cut498
  Base = -> Cylinder1305
  Tool = -> wormgear045
FEATURE [Part::Cut] Cut
  Base = -> Cut498
  Tool = -> Torus007
FEATURE [Part::Cut] Cut499
  Base = -> Cut
  Tool = -> Cylinder1304
FEATURE [Part::Compound] Compound695
  Links = -> [Cylinder1312,Cylinder1321,Cylinder1319,Cylinder1318,Cylinder1317,Cylinder1316,Cylinder1320,Cylinder1322]
FEATURE [Part::Cut] Cut496
  Base = -> Cut491
  Tool = -> Compound695
FEATURE [Part::Compound] Compound696
  Links = -> [Box418,Box419,Box425,Box420,Box424,Box421,Box422,Box423]
  Placement = pos=(0,0,-9) rot=(0,0,1;0rad)
FEATURE [Part::Cut] Cut495
  Base = -> Cut499
  Tool = -> Compound696
FEATURE [Part::Compound] Compound697
  Links = -> [Box426,Box427,Box433,Box428,Box432,Box429,Box430,Box431]
  Placement = pos=(0,0,-9) rot=(0,0,1;0rad)
FEATURE [Part::Cut] Cut493
  Base = -> Cut496
  Tool = -> Compound697
FEATURE [Part::Compound] Compound698
  Links = -> [Cylinder1308,Cylinder1314,Cylinder1313,Cylinder1310,Cylinder1315,Cylinder1307,Cylinder1311,Cylinder1309]
FEATURE [Part::Cut] Cut500
  Base = -> Cut495
  Tool = -> Compound698
FEATURE [Part::Compound] Compound694  label="J-mini_rybovina-nuovo"
  Links = -> [Cut500,Cut492,Cut493]
FEATURE [Mesh::Feature] Mesh005  label="J-mini_rybovina-nuovo (Meshed)"
FEATURE [Part::FeaturePython] Tube  label="16004"  # WARN: FeaturePython — macro-defined, semantics opaque (R4)
  AttacherType = Attacher::AttachEngine3D
  Height = 8
  InnerRadius = 10
  OuterRadius = 21
  Placement = pos=(0,0,-20) rot=(0,0,1;0rad)
FEATURE [Part::Box] Box434  label="Krychle434"
  AttacherType = Attacher::AttachEngine3D
  Height = 60
  Length = 20
  Placement = pos=(0,0,0) rot=(0,0,-1;0.383972rad)
  Width = 40
FEATURE [Part::Cylinder] Cylinder1323  label="Válec1323"
  Angle = 360
  AttacherType = Attacher::AttachEngine3D
  Height = 3
  Placement = pos=(3.5,16,55) rot=(0,0,1;0rad)
  Radius = 3
FEATURE [Part::Cylinder] Cylinder1324  label="Válec1324"
  Angle = 360
  AttacherType = Attacher::AttachEngine3D
  Height = 20
  Placement = pos=(3.5,16,40) rot=(0,0,1;0rad)
  Radius = 1.5
FEATURE [Part::Cylinder] Cylinder1325  label="Válec1325"
  Angle = 360
  AttacherType = Attacher::AttachEngine3D
  Height = 20
  Placement = pos=(-3.5,16,40) rot=(0,0,1;0rad)
  Radius = 1.5
FEATURE [Part::Compound] Compound702
  Links = -> [Cylinder1324,Cylinder1325]
  Placement = pos=(0,0,0) rot=(0,0,1;3.66519rad)
FEATURE [Part::Compound] Compound704
  Links = -> [Cylinder1324,Cylinder1325]
  Placement = pos=(0,0,0) rot=(0,0,-1;0.523599rad)
FEATURE [Part::Compound] Compound710
  Links = -> [Cylinder1324,Cylinder1325]
  Placement = pos=(0,0,0) rot=(0,0,1;1.5708rad)
FEATURE [Part::Compound] Compound706
  Links = -> [Compound704,Compound702,Compound710]
FEATURE [Part::Cylinder] Cylinder1326  label="Válec1326"
  Angle = 360
  AttacherType = Attacher::AttachEngine3D
  Height = 3
  Placement = pos=(-3.5,16,55) rot=(0,0,1;0rad)
  Radius = 3
FEATURE [Part::Compound] Compound701
  Links = -> [Cylinder1323,Cylinder1326]
  Placement = pos=(0,0,0) rot=(0,0,1;3.66519rad)
FEATURE [Part::Compound] Compound705
  Links = -> [Cylinder1323,Cylinder1326]
  Placement = pos=(0,0,0) rot=(0,0,-1;0.523599rad)
FEATURE [Part::Compound] Compound708
  Links = -> [Cylinder1323,Cylinder1326]
  Placement = pos=(0,0,0) rot=(0,0,1;1.5708rad)
FEATURE [Part::Compound] Compound699
  Links = -> [Compound705,Compound701,Compound708]
FEATURE [Part::Box] Box435  label="Krychle435"
  AttacherType = Attacher::AttachEngine3D
  Height = 60
  Length = 20
  Placement = pos=(-19.32,-5.18,0) rot=(0,0,1;0.383972rad)
  Width = 40
FEATURE [Part::Cylinder] Cylinder1327  label="Válec1327"
  Angle = 360
  AttacherType = Attacher::AttachEngine3D
  Height = 60
  Placement = pos=(-3.5,16,0) rot=(0,0,1;0rad)
  Radius = 1.5
FEATURE [Part::Cylinder] Cylinder1328  label="Válec1328"
  Angle = 360
  AttacherType = Attacher::AttachEngine3D
  Height = 5
  Placement = pos=(-8,13.8564,50) rot=(0,0,1;2.0944rad)
  Radius = 5
FEATURE [Part::Cylinder] Cylinder1329  label="Válec1329"
  Angle = 360
  AttacherType = Attacher::AttachEngine3D
  Height = 5
  Placement = pos=(-8,-13.8564,50) rot=(0,0,1;4.18879rad)
  Radius = 5
FEATURE [Part::Cylinder] Cylinder1330  label="Válec1330"
  Angle = 360
  AttacherType = Attacher::AttachEngine3D
  Height = 5
  Placement = pos=(16,0,50) rot=(0,0,1;0rad)
  Radius = 5
FEATURE [Part::Compound] Compound709
  Links = -> [Cylinder1329,Cylinder1328,Cylinder1330]
FEATURE [Part::Cylinder] Cylinder1331  label="Válec1331"
  Angle = 360
  AttacherType = Attacher::AttachEngine3D
  Height = 16
  Placement = pos=(0,0,48) rot=(0,0,1;0rad)
  Radius = 8
FEATURE [Part::Box] Box436  label="Krychle436"
  AttacherType = Attacher::AttachEngine3D
  Height = 60
  Length = 60
  Placement = pos=(-30,-35,0) rot=(0,0,1;0rad)
  Width = 40
FEATURE [Part::Cylinder] Cylinder1332  label="Válec1332"
  Angle = 360
  AttacherType = Attacher::AttachEngine3D
  Height = 60
  Placement = pos=(3.5,16,0) rot=(0,0,1;0rad)
  Radius = 1.5
FEATURE [Part::Compound] Compound703
  Links = -> [Cylinder1332,Cylinder1327]
FEATURE [Part::Cylinder] Cylinder1333  label="Válec1333"
  Angle = 360
  AttacherType = Attacher::AttachEngine3D
  Height = 8
  Placement = pos=(0,0,50) rot=(0,0,1;0rad)
  Radius = 24
FEATURE [Part::Cut] Cut506
  Base = -> Cylinder1333
  Tool = -> Cylinder1331
FEATURE [Part::Cut] Cut505
  Base = -> Cut506
  Tool = -> Compound709
FEATURE [Part::Cut] Cut509
  Base = -> Cut505
  Tool = -> Compound699
FEATURE [Part::Cut] Cut501
  Base = -> Cut509
  Tool = -> Compound706
FEATURE [Part::FeaturePython] Tube055  # WARN: FeaturePython — macro-defined, semantics opaque (R4)
  AttacherType = Attacher::AttachEngine3D
  Height = 1
  InnerRadius = 4.5
  OuterRadius = 5
  Placement = pos=(16,0,54) rot=(0,0,1;0rad)
FEATURE [Part::FeaturePython] Tube056  # WARN: FeaturePython — macro-defined, semantics opaque (R4)
  AttacherType = Attacher::AttachEngine3D
  Height = 1
  InnerRadius = 4.5
  OuterRadius = 5
  Placement = pos=(-8,-13.8564,54) rot=(0,0,1;4.18879rad)
FEATURE [Part::FeaturePython] Tube057  # WARN: FeaturePython — macro-defined, semantics opaque (R4)
  AttacherType = Attacher::AttachEngine3D
  Height = 1
  InnerRadius = 4.5
  OuterRadius = 5
  Placement = pos=(-8,13.8564,54) rot=(0,0,1;2.0944rad)
FEATURE [Part::Compound] Compound707
  Links = -> [Tube057,Tube056,Tube055]
FEATURE [Part::Compound] Compound711  label="jointovina_micro_pikovina002"
  Links = -> [Compound707,Cut501]
FEATURE [Part::FeaturePython] Tube058  # WARN: FeaturePython — macro-defined, semantics opaque (R4)
  AttacherType = Attacher::AttachEngine3D
  Height = 27
  InnerRadius = 12
  OuterRadius = 20.5
  Placement = pos=(0,0,23) rot=(0,0,1;0rad)
FEATURE [Part::Cut] Cut502
  Base = -> Tube058
  Tool = -> Box436
FEATURE [Part::Cut] Cut503
  Base = -> Cut502
  Tool = -> Box435
FEATURE [Part::Cut] Cut507
  Base = -> Cut503
  Tool = -> Box434
FEATURE [Part::Cut] Cut504
  Base = -> Cut507
  Placement = pos=(0,0,0) rot=(0,0,-1;0.523599rad)
  Tool = -> Compound703
FEATURE [Part::Cut] Cut508
  Base = -> Cut507
  Placement = pos=(0,0,0) rot=(0,0,1;3.66519rad)
  Tool = -> Compound703
FEATURE [Part::Cut] Cut510
  Base = -> Cut507
  Placement = pos=(0,0,0) rot=(0,0,1;1.5708rad)
  Tool = -> Compound703
FEATURE [Part::Compound] Compound700  label="J-mini_pikovina1"
  Links = -> [Compound711,Cut504,Cut510,Cut508]
FEATURE [Part::FeaturePython] Tube039  # WARN: FeaturePython — macro-defined, semantics opaque (R4)
  AttacherType = Attacher::AttachEngine3D
  Height = 1
  InnerRadius = 8
  OuterRadius = 13
  Placement = pos=(0,0,58) rot=(0,0,1;0rad)
FEATURE [Part::FeaturePython] Tube038  # WARN: FeaturePython — macro-defined, semantics opaque (R4)
  AttacherType = Attacher::AttachEngine3D
  Height = 8
  InnerRadius = 8
  OuterRadius = 10
  Placement = pos=(0,0,58) rot=(0,0,1;0rad)
FEATURE [Part::Chamfer] Chamfer013
  Base = -> Tube038
  Edges = 1 edges r=0.5: [Edge1]
FEATURE [Part::Compound] Compound712  label="J-mini_pikovina-fixo"
  Links = -> [Compound700,Tube039,Chamfer013]
FEATURE [Mesh::Feature] Mesh006  label="J-mini_pikovina-fixo (Meshed)"
FEATURE [Part::FeaturePython] Tube041  # WARN: FeaturePython — macro-defined, semantics opaque (R4)
  AttacherType = Attacher::AttachEngine3D
  Height = 1
  InnerRadius = 4.5
  OuterRadius = 5
  Placement = pos=(-8,-13.8564,54) rot=(0,0,1;4.18879rad)
FEATURE [Part::FeaturePython] Tube042  # WARN: FeaturePython — macro-defined, semantics opaque (R4)
  AttacherType = Attacher::AttachEngine3D
  Height = 1
  InnerRadius = 4.5
  OuterRadius = 5
  Placement = pos=(-8,13.8564,54) rot=(0,0,1;2.0944rad)
FEATURE [Part::FeaturePython] Tube046  # WARN: FeaturePython — macro-defined, semantics opaque (R4)
  AttacherType = Attacher::AttachEngine3D
  Height = 1
  InnerRadius = 7
  OuterRadius = 8
  Placement = pos=(0,0,55) rot=(0,0,1;0rad)
FEATURE [Part::FeaturePython] Tube083  # WARN: FeaturePython — macro-defined, semantics opaque (R4)
  AttacherType = Attacher::AttachEngine3D
  Height = 1
  InnerRadius = 6
  OuterRadius = 8
  Placement = pos=(0,0,58) rot=(0,0,1;0rad)
FEATURE [Part::FeaturePython] Tube084  # WARN: FeaturePython — macro-defined, semantics opaque (R4)
  AttacherType = Attacher::AttachEngine3D
  Height = 1
  InnerRadius = 4.5
  OuterRadius = 5
  Placement = pos=(16,0,54) rot=(0,0,1;0rad)
FEATURE [Part::Cylinder] Cylinder1203  label="Válec1203"
  Angle = 360
  AttacherType = Attacher::AttachEngine3D
  Height = 5
  Placement = pos=(-8,-13.8564,50) rot=(0,0,1;4.18879rad)
  Radius = 5
FEATURE [Part::Cylinder] Cylinder1195  label="Válec1195"
  Angle = 360
  AttacherType = Attacher::AttachEngine3D
  Height = 16
  Placement = pos=(0,0,100) rot=(0,0,1;0rad)
  Radius = 8
FEATURE [Part::Cylinder] Cylinder1196  label="Válec1196"
  Angle = 360
  AttacherType = Attacher::AttachEngine3D
  Height = 5
  Placement = pos=(-8,13.8564,50) rot=(0,0,1;2.0944rad)
  Radius = 5
FEATURE [Part::Cylinder] Cylinder1197  label="Válec1197"
  Angle = 360
  AttacherType = Attacher::AttachEngine3D
  Height = 5
  Placement = pos=(16,0,50) rot=(0,0,1;0rad)
  Radius = 5
FEATURE [Part::Cylinder] Cylinder1198  label="Válec1198"
  Angle = 360
  AttacherType = Attacher::AttachEngine3D
  Height = 8
  Placement = pos=(0,0,50) rot=(0,0,1;0rad)
  Radius = 24
FEATURE [Part::Cut] Cut442
  Base = -> Cylinder1198
  Tool = -> Cylinder1195
FEATURE [Part::Cylinder] Cylinder1200  label="Válec1200"
  Angle = 360
  AttacherType = Attacher::AttachEngine3D
  Height = 3
  Placement = pos=(-3.5,16,55) rot=(0,0,1;0rad)
  Radius = 3
FEATURE [Part::Cylinder] Cylinder1199  label="Válec1199"
  Angle = 360
  AttacherType = Attacher::AttachEngine3D
  Height = 3
  Placement = pos=(3.5,16,55) rot=(0,0,1;0rad)
  Radius = 3
FEATURE [Part::Cylinder] Cylinder1202  label="Válec1202"
  Angle = 360
  AttacherType = Attacher::AttachEngine3D
  Height = 20
  Placement = pos=(3.5,16,40) rot=(0,0,1;0rad)
  Radius = 1.5
FEATURE [Part::Cylinder] Cylinder829  label="Válec829"
  Angle = 360
  AttacherType = Attacher::AttachEngine3D
  Height = 6
  Placement = pos=(0,0,50) rot=(0,0,1;0rad)
  Radius = 8
FEATURE [Part::Cylinder] Cylinder1920  label="Válec1920"
  Angle = 360
  AttacherType = Attacher::AttachEngine3D
  Height = 8
  Placement = pos=(0,0,88) rot=(0,0,1;0rad)
  Radius = 6
FEATURE [Part::Cylinder] Cylinder1205  label="Válec1205"
  Angle = 360
  AttacherType = Attacher::AttachEngine3D
  Height = 20
  Placement = pos=(-3.5,16,40) rot=(0,0,1;0rad)
  Radius = 1.5
FEATURE [Part::Compound] Compound649
  Links = -> [Tube042,Tube041,Tube084]
FEATURE [Part::Compound] Compound650
  Links = -> [Cylinder1202,Cylinder1205]
  Placement = pos=(0,0,0) rot=(0,0,1;1.5708rad)
FEATURE [Part::Compound] Compound645
  Links = -> [Cylinder1202,Cylinder1205]
  Placement = pos=(0,0,0) rot=(0,0,1;3.66519rad)
FEATURE [Part::Compound] Compound638
  Links = -> [Cylinder1203,Cylinder1196,Cylinder1197]
FEATURE [Part::Cut] Cut445
  Base = -> Cut442
  Tool = -> Compound638
FEATURE [Part::Compound] Compound639
  Links = -> [Cylinder1199,Cylinder1200]
  Placement = pos=(0,0,0) rot=(0,0,-1;0.523599rad)
FEATURE [Part::Compound] Compound642
  Links = -> [Cylinder1199,Cylinder1200]
  Placement = pos=(0,0,0) rot=(0,0,1;1.5708rad)
FEATURE [Part::Compound] Compound643
  Links = -> [Cylinder1202,Cylinder1205]
  Placement = pos=(0,0,0) rot=(0,0,-1;0.523599rad)
FEATURE [Part::Compound] Compound646
  Links = -> [Compound643,Compound645,Compound650]
FEATURE [Part::Compound] Compound644
  Links = -> [Cylinder1199,Cylinder1200]
  Placement = pos=(0,0,0) rot=(0,0,1;3.66519rad)
FEATURE [Part::Compound] Compound641
  Links = -> [Compound639,Compound644,Compound642]
FEATURE [Part::Cut] Cut443
  Base = -> Cut445
  Tool = -> Compound641
FEATURE [Part::Cut] Cut447
  Base = -> Cut443
  Tool = -> Compound646
FEATURE [Part::Compound] Compound640  label="jointovina_micro_quikovina1"
  Links = -> [Compound649,Cut447]
FEATURE [Part::Cut] Cut448
  Base = -> Compound640
  Tool = -> Cylinder829
FEATURE [Part::Compound] Compound651  label="jointovina_micro_quikovina"
  Links = -> [Cut448,Tube046]
FEATURE [Part::Chamfer] Chamfer014
  Base = -> Cylinder1920
  Edges = 1 edges r=1: [Edge1]
  Placement = pos=(0,0,-30) rot=(0,0,1;0rad)
FEATURE [Part::Compound] Compound874  label="J-mini_quikovina"
  Links = -> [Compound651,Chamfer014,Tube083]
  Placement = pos=(0,0,-58) rot=(0,0,1;0rad)
FEATURE [Mesh::Feature] Mesh007  label="J-mini_quikovina (Meshed)"
FEATURE [Part::Torus] Torus002  label="Anuloid002"
  Angle1 = -180
  Angle2 = 180
  Angle3 = 360
  AttacherType = Attacher::AttachEngine3D
  Placement = pos=(0,0,20) rot=(0,0,1;0rad)
  Radius1 = 32
  Radius2 = 3.1
FEATURE [Part::FeaturePython] Tube011  # WARN: FeaturePython — macro-defined, semantics opaque (R4)
  AttacherType = Attacher::AttachEngine3D
  Height = 13
  InnerRadius = 33
  OuterRadius = 40
  Placement = pos=(0,0,12) rot=(0,0,1;0rad)
FEATURE [Part::Cut] Cut166
  Base = -> Tube011
  Tool = -> Torus002
FEATURE [Part::Box] Box079  label="Krychle079"
  AttacherType = Attacher::AttachEngine3D
  Height = 2
  Length = 8
  Placement = pos=(3,33,14) rot=(0,0,1;1.5708rad)
  Width = 6
FEATURE [Part::Cylinder] Cylinder231  label="Válec231"
  Angle = 360
  AttacherType = Attacher::AttachEngine3D
  Height = 18
  Placement = pos=(25.4558,25.4558,0) rot=(0,0,1;0.785398rad)
  Radius = 1.5
FEATURE [Part::Box] Box080  label="Krychle080"
  AttacherType = Attacher::AttachEngine3D
  Height = 2
  Length = 8
  Placement = pos=(-21.21,25.46,14) rot=(0,0,1;2.35619rad)
  Width = 6
FEATURE [Part::Cylinder] Cylinder246  label="Válec246"
  Angle = 360
  AttacherType = Attacher::AttachEngine3D
  Height = 20
  Placement = pos=(31,21,22) rot=(0,1,0;1.5708rad)
  Radius = 1.5
FEATURE [Part::Box] Box081  label="Krychle081"
  AttacherType = Attacher::AttachEngine3D
  Height = 2
  Length = 8
  Placement = pos=(-33,3,14) rot=(0,0,1;3.14159rad)
  Width = 6
FEATURE [Part::Box] Box082  label="Krychle082"
  AttacherType = Attacher::AttachEngine3D
  Height = 2
  Length = 8
  Placement = pos=(-25.46,-21.21,14) rot=(0,0,1;3.92699rad)
  Width = 6
FEATURE [Part::Box] Box078  label="Krychle078"
  AttacherType = Attacher::AttachEngine3D
  Height = 2
  Length = 8
  Placement = pos=(25.46,21.21,14) rot=(0,0,1;0.785398rad)
  Width = 6
FEATURE [Part::Box] Box077  label="Krychle077"
  AttacherType = Attacher::AttachEngine3D
  Height = 2
  Length = 8
  Placement = pos=(33,-3,14) rot=(0,0,1;0rad)
  Width = 6
FEATURE [Part::Box] Box083  label="Krychle083"
  AttacherType = Attacher::AttachEngine3D
  Height = 2
  Length = 8
  Placement = pos=(-3,-33,14) rot=(0,0,-1;1.5708rad)
  Width = 6
FEATURE [Part::Box] Box084  label="Krychle084"
  AttacherType = Attacher::AttachEngine3D
  Height = 2
  Length = 8
  Placement = pos=(21.21,-25.46,14) rot=(0,0,-1;0.785398rad)
  Width = 6
FEATURE [Part::Cylinder] Cylinder230  label="Válec230"
  Angle = 360
  AttacherType = Attacher::AttachEngine3D
  Height = 18
  Placement = pos=(36,0,0) rot=(0,0,1;0rad)
  Radius = 1.5
FEATURE [Part::Cylinder] Cylinder235  label="Válec235"
  Angle = 360
  AttacherType = Attacher::AttachEngine3D
  Height = 18
  Placement = pos=(-25.4558,-25.4558,0) rot=(0,0,1;3.92699rad)
  Radius = 1.5
FEATURE [Part::Box] Box092  label="Krychle092"
  AttacherType = Attacher::AttachEngine3D
  Height = 6
  Length = 2
  Placement = pos=(34,18,19) rot=(0,0,1;0rad)
  Width = 6
FEATURE [Part::Cylinder] Cylinder245  label="Válec245"
  Angle = 360
  AttacherType = Attacher::AttachEngine3D
  Height = 20
  Placement = pos=(26,37,19) rot=(0,1,0;1.5708rad)
  Radius = 1.5
FEATURE [Part::Cylinder] Cylinder234  label="Válec234"
  Angle = 360
  AttacherType = Attacher::AttachEngine3D
  Height = 18
  Placement = pos=(-36,-1.1e-14,0) rot=(0,0,1;3.14159rad)
  Radius = 1.5
FEATURE [Part::Box] Box091  label="Krychle091"
  AttacherType = Attacher::AttachEngine3D
  Height = 6
  Length = 2
  Placement = pos=(30,34,16) rot=(0,0,1;0rad)
  Width = 6
FEATURE [Part::Cylinder] Cylinder248  label="Válec248"
  Angle = 360
  AttacherType = Attacher::AttachEngine3D
  Height = 20
  Placement = pos=(26,-37,19) rot=(0,1,0;1.5708rad)
  Radius = 1.5
FEATURE [Part::Box] Box094  label="Krychle094"
  AttacherType = Attacher::AttachEngine3D
  Height = 6
  Length = 2
  Placement = pos=(34,-24,19) rot=(0,0,1;0rad)
  Width = 6
FEATURE [Part::Box] Box093  label="Krychle093"
  AttacherType = Attacher::AttachEngine3D
  Height = 6
  Length = 2
  Placement = pos=(30,-40,16) rot=(0,0,1;0rad)
  Width = 6
FEATURE [Part::Box] Box090  label="Krychle090"
  AttacherType = Attacher::AttachEngine3D
  Height = 13
  Length = 40
  Placement = pos=(0,-40,12) rot=(0,0,1;0rad)
  Width = 80
FEATURE [Part::Cylinder] Cylinder247  label="Válec247"
  Angle = 360
  AttacherType = Attacher::AttachEngine3D
  Height = 20
  Placement = pos=(31,-21,22) rot=(0,1,0;1.5708rad)
  Radius = 1.5
FEATURE [Part::Cylinder] Cylinder232  label="Válec232"
  Angle = 360
  AttacherType = Attacher::AttachEngine3D
  Height = 18
  Placement = pos=(-4e-15,36,0) rot=(0,0,1;1.5708rad)
  Radius = 1.5
FEATURE [Part::Cylinder] Cylinder233  label="Válec233"
  Angle = 360
  AttacherType = Attacher::AttachEngine3D
  Height = 18
  Placement = pos=(-25.4558,25.4558,0) rot=(0,0,1;2.35619rad)
  Radius = 1.5
FEATURE [Part::Cylinder] Cylinder236  label="Válec236"
  Angle = 360
  AttacherType = Attacher::AttachEngine3D
  Height = 18
  Placement = pos=(1.2e-14,-36,0) rot=(0,0,-1;1.5708rad)
  Radius = 1.5
FEATURE [Part::Compound] Compound145
  Links = -> [Box091,Box092,Box093,Box094]
FEATURE [Part::Compound] Compound136
  Links = -> [Box077,Box078,Box079,Box080,Box081,Box082,Box083,Box084]
FEATURE [Part::Cut] Cut167
  Base = -> Cut166
  Tool = -> Compound136
FEATURE [Part::Compound] Compound146
  Links = -> [Cylinder245,Cylinder246,Cylinder247,Cylinder248]
FEATURE [Part::Cylinder] Cylinder252  label="Válec252"
  Angle = 360
  AttacherType = Attacher::AttachEngine3D
  Height = 20
  Placement = pos=(26,-37,19) rot=(0,1,0;1.5708rad)
  Radius = 1.5
FEATURE [Part::Box] Box097  label="Krychle097"
  AttacherType = Attacher::AttachEngine3D
  Height = 6
  Length = 2
  Placement = pos=(34,-24,19) rot=(0,0,1;0rad)
  Width = 6
FEATURE [Part::Box] Box096  label="Krychle096"
  AttacherType = Attacher::AttachEngine3D
  Height = 6
  Length = 2
  Placement = pos=(34,18,19) rot=(0,0,1;0rad)
  Width = 6
FEATURE [Part::Cylinder] Cylinder238  label="Válec238"
  Angle = 360
  AttacherType = Attacher::AttachEngine3D
  Height = 10
  Placement = pos=(0,-31.6,20) rot=(0,0,1;0rad)
  Radius = 3.5
FEATURE [Part::Cylinder] Cylinder237  label="Válec237"
  Angle = 360
  AttacherType = Attacher::AttachEngine3D
  Height = 18
  Placement = pos=(25.4558,-25.4558,0) rot=(0,0,-1;0.785398rad)
  Radius = 1.5
FEATURE [Part::Compound] Compound137
  Links = -> [Cylinder231,Cylinder232,Cylinder233,Cylinder234,Cylinder235,Cylinder236,Cylinder237,Cylinder230]
FEATURE [Part::Cut] Cut168
  Base = -> Cut167
  Tool = -> Compound137
FEATURE [Part::Cylinder] Cylinder251  label="Válec251"
  Angle = 360
  AttacherType = Attacher::AttachEngine3D
  Height = 20
  Placement = pos=(31,-21,22) rot=(0,1,0;1.5708rad)
  Radius = 1.5
FEATURE [Part::Box] Box095  label="Krychle095"
  AttacherType = Attacher::AttachEngine3D
  Height = 6
  Length = 2
  Placement = pos=(30,34,16) rot=(0,0,1;0rad)
  Width = 6
FEATURE [Part::Cylinder] Cylinder244  label="Válec244"
  Angle = 360
  AttacherType = Attacher::AttachEngine3D
  Height = 13
  Placement = pos=(0,0,12) rot=(0,0,1;0rad)
  Radius = 40
FEATURE [Part::Cut] Cut173
  Base = -> Box090
  Tool = -> Cylinder244
FEATURE [Part::Cut] Cut174
  Base = -> Cut173
  Tool = -> Compound145
FEATURE [Part::Cut] Cut175
  Base = -> Cut174
  Tool = -> Compound146
FEATURE [Part::Cylinder] Cylinder249  label="Válec249"
  Angle = 360
  AttacherType = Attacher::AttachEngine3D
  Height = 20
  Placement = pos=(31,21,22) rot=(0,1,0;1.5708rad)
  Radius = 1.5
FEATURE [Part::Box] Box098  label="Krychle098"
  AttacherType = Attacher::AttachEngine3D
  Height = 6
  Length = 2
  Placement = pos=(30,-40,16) rot=(0,0,1;0rad)
  Width = 6
FEATURE [Part::Compound] Compound147
  Links = -> [Box095,Box096,Box098,Box097]
FEATURE [Part::Cylinder] Cylinder250  label="Válec250"
  Angle = 360
  AttacherType = Attacher::AttachEngine3D
  Height = 20
  Placement = pos=(26,37,19) rot=(0,1,0;1.5708rad)
  Radius = 1.5
FEATURE [Part::Compound] Compound148
  Links = -> [Cylinder250,Cylinder249,Cylinder251,Cylinder252]
FEATURE [Part::Cut] Cut169
  Base = -> Cut168
  Tool = -> Cylinder238
FEATURE [Part::Cut] Cut176
  Base = -> Cut169
  Tool = -> Compound147
FEATURE [Part::Cut] Cut177
  Base = -> Cut176
  Tool = -> Compound148
FEATURE [Part::Compound] Compound149  label="J-mini_bearing-ring"
  Links = -> [Cut177,Cut175]
FEATURE [Part::FeaturePython] wormgear047  # WARN: FeaturePython — macro-defined, semantics opaque (R4)
  AttacherType = Attacher::AttachEngine3D
  Placement = pos=(0,0,0) rot=(0,0,1;0.011345rad)
  beta = 36.5317
  clearance = 0.25
  diameter = 49
  head = 0
  height = 20
  module = 1.1
  pressure_angle = 20
  reverse_pitch = true
  teeth = 33
  version = 0.0.3
FEATURE [Part::FeaturePython] wormgear048  # WARN: FeaturePython — macro-defined, semantics opaque (R4)
  AttacherType = Attacher::AttachEngine3D
  Placement = pos=(0,0,0) rot=(0,0,1;0.043633rad)
  beta = 36.5317
  clearance = 0.25
  diameter = 49
  head = 0
  height = 20
  module = 1.1
  pressure_angle = 20
  reverse_pitch = false
  teeth = 33
  version = 0.0.3
FEATURE [Part::FeaturePython] Tube085  # WARN: FeaturePython — macro-defined, semantics opaque (R4)
  AttacherType = Attacher::AttachEngine3D
  Height = 6
  InnerRadius = 26
  OuterRadius = 32
  Placement = pos=(0,0,-6) rot=(0,0,1;0rad)
FEATURE [Part::Cylinder] Cylinder1921  label="Válec1921"
  Angle = 360
  AttacherType = Attacher::AttachEngine3D
  Height = 6
  Radius = 32
FEATURE [Part::Cylinder] Cylinder1922  label="Válec1922"
  Angle = 360
  AttacherType = Attacher::AttachEngine3D
  Height = 20
  Placement = pos=(11.0978,26.7925,-10) rot=(0,0,1;1.1781rad)
  Radius = 1.5
FEATURE [Part::Cylinder] Cylinder1923  label="Válec1923"
  Angle = 360
  AttacherType = Attacher::AttachEngine3D
  Height = 20
  Placement = pos=(36,0,0) rot=(0,0,1;0rad)
  Radius = 1.5
FEATURE [Part::Cylinder] Cylinder1924  label="Válec1924"
  Angle = 360
  AttacherType = Attacher::AttachEngine3D
  Height = 20
  Placement = pos=(25.4558,-25.4558,0) rot=(0,0,-1;0.785398rad)
  Radius = 1.5
FEATURE [Part::Cylinder] Cylinder1925  label="Válec1925"
  Angle = 360
  AttacherType = Attacher::AttachEngine3D
  Height = 20
  Placement = pos=(-26.7925,11.0978,-10) rot=(0,0,1;2.74889rad)
  Radius = 1.5
FEATURE [Part::Cylinder] Cylinder1926  label="Válec1926"
  Angle = 360
  AttacherType = Attacher::AttachEngine3D
  Height = 20
  Placement = pos=(-11.0978,-26.7925,-10) rot=(0,0,-1;1.96349rad)
  Radius = 1.5
FEATURE [Part::Cylinder] Cylinder1927  label="Válec1927"
  Angle = 360
  AttacherType = Attacher::AttachEngine3D
  Height = 20
  Placement = pos=(26.7925,-11.0978,-10) rot=(0,0,-1;0.392699rad)
  Radius = 1.5
FEATURE [Part::Cylinder] Cylinder1928  label="Válec1928"
  Angle = 360
  AttacherType = Attacher::AttachEngine3D
  Height = 6
  Radius = 40
FEATURE [Part::Cylinder] Cylinder1929  label="Válec1929"
  Angle = 360
  AttacherType = Attacher::AttachEngine3D
  Height = 20
  Placement = pos=(25.4558,25.4558,0) rot=(0,0,1;0.785398rad)
  Radius = 1.5
FEATURE [Part::Cylinder] Cylinder1930  label="Válec1930"
  Angle = 360
  AttacherType = Attacher::AttachEngine3D
  Height = 20
  Placement = pos=(11.0978,-26.7925,-10) rot=(0,0,-1;1.1781rad)
  Radius = 1.5
FEATURE [Part::Cylinder] Cylinder1931  label="Válec1931"
  Angle = 360
  AttacherType = Attacher::AttachEngine3D
  Height = 20
  Placement = pos=(26.7925,11.0978,-10) rot=(0,0,1;0.392699rad)
  Radius = 1.5
FEATURE [Part::Cylinder] Cylinder1932  label="Válec1932"
  Angle = 360
  AttacherType = Attacher::AttachEngine3D
  Height = 20
  Placement = pos=(-11.0978,26.7925,-10) rot=(0,0,1;1.96349rad)
  Radius = 1.5
FEATURE [Part::Cylinder] Cylinder1933  label="Válec1933"
  Angle = 360
  AttacherType = Attacher::AttachEngine3D
  Height = 20
  Placement = pos=(-25.4558,-25.4558,0) rot=(0,0,1;3.92699rad)
  Radius = 1.5
FEATURE [Part::Cylinder] Cylinder1934  label="Válec1934"
  Angle = 360
  AttacherType = Attacher::AttachEngine3D
  Height = 20
  Placement = pos=(-26.7925,-11.0978,-10) rot=(0,0,1;3.53429rad)
  Radius = 1.5
FEATURE [Part::Compound] Compound135
  Links = -> [Cylinder1931,Cylinder1922,Cylinder1932,Cylinder1925,Cylinder1934,Cylinder1926,Cylinder1930,Cylinder1927]
FEATURE [Part::Cut] Cut513
  Base = -> Cylinder1921
  Tool = -> wormgear048
FEATURE [Part::Cut] Cut511
  Base = -> Cut513
  Tool = -> Compound135
FEATURE [Part::Cut] Cut528
  Base = -> Cylinder1928
  Placement = pos=(0,0,6) rot=(0,0,-1;0.017453rad)
  Tool = -> wormgear047
FEATURE [Part::Cylinder] Cylinder1935  label="Válec1935"
  Angle = 360
  AttacherType = Attacher::AttachEngine3D
  Height = 20
  Placement = pos=(26.7925,-11.0978,-10) rot=(0,0,-1;0.392699rad)
  Radius = 1.5
FEATURE [Part::Box] Box437  label="Krychle437"
  AttacherType = Attacher::AttachEngine3D
  Height = 2
  Length = 6
  Placement = pos=(-7.17813,25.1689,-2) rot=(0,0,1;1.96349rad)
  Width = 6
FEATURE [Part::Box] Box438  label="Krychle438"
  AttacherType = Attacher::AttachEngine3D
  Height = 6
  Length = 2
  Placement = pos=(30,34,4) rot=(0,0,1;0rad)
  Width = 6
FEATURE [Part::Box] Box439  label="Krychle439"
  AttacherType = Attacher::AttachEngine3D
  Height = 6
  Length = 40
  Placement = pos=(0,0,6) rot=(0,0,1;0rad)
  Width = 40
FEATURE [Part::Cylinder] Cylinder1936  label="Válec1936"
  Angle = 360
  AttacherType = Attacher::AttachEngine3D
  Height = 20
  Placement = pos=(-26.7925,11.0978,-10) rot=(0,0,1;2.74889rad)
  Radius = 1.5
FEATURE [Part::Box] Box440  label="Krychle440"
  AttacherType = Attacher::AttachEngine3D
  Height = 2
  Length = 6
  Placement = pos=(22.8728,-12.7214,-2) rot=(0,0,-1;0.392699rad)
  Width = 6
FEATURE [Part::Cylinder] Cylinder1937  label="Válec1937"
  Angle = 360
  AttacherType = Attacher::AttachEngine3D
  Height = 20
  Placement = pos=(-25.4558,25.4558,0) rot=(0,0,1;2.35619rad)
  Radius = 1.5
FEATURE [Part::Cylinder] Cylinder1938  label="Válec1938"
  Angle = 360
  AttacherType = Attacher::AttachEngine3D
  Height = 20
  Placement = pos=(11.0978,-26.7925,-10) rot=(0,0,-1;1.1781rad)
  Radius = 1.5
FEATURE [Part::Cylinder] Cylinder1939  label="Válec1939"
  Angle = 360
  AttacherType = Attacher::AttachEngine3D
  Height = 30
  Placement = pos=(25.4558,25.4558,-24) rot=(0,0,1;0.785398rad)
  Radius = 4
FEATURE [Part::Box] Box441  label="Krychle441"
  AttacherType = Attacher::AttachEngine3D
  Height = 18
  Length = 14
  Placement = pos=(26,0,-6) rot=(0,0,1;0rad)
  Width = 40
FEATURE [Part::Box] Box442  label="Krychle442"
  AttacherType = Attacher::AttachEngine3D
  Height = 2
  Length = 6
  Placement = pos=(12.7214,22.8728,-2) rot=(0,0,1;1.1781rad)
  Width = 6
FEATURE [Part::Cylinder] Cylinder1940  label="Válec1940"
  Angle = 360
  AttacherType = Attacher::AttachEngine3D
  Height = 20
  Placement = pos=(-4e-15,36,0) rot=(0,0,1;1.5708rad)
  Radius = 1.5
FEATURE [Part::Cylinder] Cylinder1941  label="Válec1941"
  Angle = 360
  AttacherType = Attacher::AttachEngine3D
  Height = 20
  Placement = pos=(26.7925,11.0978,-10) rot=(0,0,1;0.392699rad)
  Radius = 1.5
FEATURE [Part::Box] Box443  label="Krychle443"
  AttacherType = Attacher::AttachEngine3D
  Height = 2
  Length = 6
  Placement = pos=(25.1689,7.17813,-2) rot=(0,0,1;0.392699rad)
  Width = 6
FEATURE [Part::Cylinder] Cylinder1942  label="Válec1942"
  Angle = 360
  AttacherType = Attacher::AttachEngine3D
  Height = 20
  Placement = pos=(25.4558,25.4558,0) rot=(0,0,1;0.785398rad)
  Radius = 1.5
FEATURE [Part::Box] Box444  label="Krychle444"
  AttacherType = Attacher::AttachEngine3D
  Height = 6
  Length = 2
  Placement = pos=(30,34,4) rot=(0,0,1;0rad)
  Width = 6
FEATURE [Part::Box] Box445  label="Krychle445"
  AttacherType = Attacher::AttachEngine3D
  Height = 2
  Length = 6
  Placement = pos=(-25.1689,-7.17813,-2) rot=(0,0,1;3.53429rad)
  Width = 6
FEATURE [Part::Cylinder] Cylinder1943  label="Válec1943"
  Angle = 360
  AttacherType = Attacher::AttachEngine3D
  Height = 20
  Placement = pos=(-11.0978,26.7925,-10) rot=(0,0,1;1.96349rad)
  Radius = 1.5
FEATURE [Part::Cylinder] Cylinder1944  label="Válec1944"
  Angle = 360
  AttacherType = Attacher::AttachEngine3D
  Height = 20
  Placement = pos=(-36,-1.1e-14,0) rot=(0,0,1;3.14159rad)
  Radius = 1.5
FEATURE [Part::Cylinder] Cylinder1945  label="Válec1945"
  Angle = 360
  AttacherType = Attacher::AttachEngine3D
  Height = 20
  Placement = pos=(11.0978,26.7925,-10) rot=(0,0,1;1.1781rad)
  Radius = 1.5
FEATURE [Part::Box] Box446  label="Krychle446"
  AttacherType = Attacher::AttachEngine3D
  Height = 2
  Length = 6
  Placement = pos=(-12.7214,-22.8728,-2) rot=(0,0,-1;1.96349rad)
  Width = 6
FEATURE [Part::Box] Box447  label="Krychle447"
  AttacherType = Attacher::AttachEngine3D
  Height = 2
  Length = 6
  Placement = pos=(-22.8728,12.7214,-2) rot=(0,0,1;2.74889rad)
  Width = 6
FEATURE [Part::Cylinder] Cylinder1946  label="Válec1946"
  Angle = 360
  AttacherType = Attacher::AttachEngine3D
  Height = 20
  Placement = pos=(-11.0978,-26.7925,-10) rot=(0,0,-1;1.96349rad)
  Radius = 1.5
FEATURE [Part::Cylinder] Cylinder1947  label="Válec1947"
  Angle = 360
  AttacherType = Attacher::AttachEngine3D
  Height = 6
  Placement = pos=(0,0,6) rot=(0,0,1;0rad)
  Radius = 40
FEATURE [Part::Cut] Cut516
  Base = -> Box439
  Tool = -> Cylinder1947
FEATURE [Part::Cut] Cut522
  Base = -> Cut516
  Tool = -> Box438
FEATURE [Part::Cylinder] Cylinder1948  label="Válec1948"
  Angle = 360
  AttacherType = Attacher::AttachEngine3D
  Height = 20
  Placement = pos=(36,0,0) rot=(0,0,1;0rad)
  Radius = 1.5
FEATURE [Part::Box] Box448  label="Krychle448"
  AttacherType = Attacher::AttachEngine3D
  Height = 6
  Length = 40
  Placement = pos=(0,0,6) rot=(0,0,1;0rad)
  Width = 40
FEATURE [Part::Cylinder] Cylinder1949  label="Válec1949"
  Angle = 360
  AttacherType = Attacher::AttachEngine3D
  Height = 20
  Placement = pos=(26,37,7) rot=(0,1,0;1.5708rad)
  Radius = 1.5
FEATURE [Part::Box] Box449  label="Krychle449"
  AttacherType = Attacher::AttachEngine3D
  Height = 2
  Length = 6
  Placement = pos=(7.17813,-25.1689,-2) rot=(0,0,-1;1.1781rad)
  Width = 6
FEATURE [Part::Cylinder] Cylinder1950  label="Válec1950"
  Angle = 360
  AttacherType = Attacher::AttachEngine3D
  Height = 30
  Placement = pos=(25.4558,25.4558,-24) rot=(0,0,1;0.785398rad)
  Radius = 4
FEATURE [Part::Box] Box450  label="Krychle450"
  AttacherType = Attacher::AttachEngine3D
  Height = 12
  Length = 18
  Placement = pos=(8,10,-6) rot=(0,0,1;0rad)
  Width = 30
FEATURE [Part::Cylinder] Cylinder1951  label="Válec1951"
  Angle = 360
  AttacherType = Attacher::AttachEngine3D
  Height = 12
  Placement = pos=(0,0,-6) rot=(0,0,1;0rad)
  Radius = 32
FEATURE [Part::Cylinder] Cylinder1952  label="Válec1952"
  Angle = 360
  AttacherType = Attacher::AttachEngine3D
  Height = 20
  Placement = pos=(-26.7925,-11.0978,-10) rot=(0,0,1;3.53429rad)
  Radius = 1.5
FEATURE [Part::Cylinder] Cylinder1953  label="Válec1953"
  Angle = 360
  AttacherType = Attacher::AttachEngine3D
  Height = 20
  Placement = pos=(26,37,7) rot=(0,1,0;1.5708rad)
  Radius = 1.5
FEATURE [Part::Cylinder] Cylinder1954  label="Válec1954"
  Angle = 360
  AttacherType = Attacher::AttachEngine3D
  Height = 30
  Placement = pos=(36,0,-24) rot=(0,0,1;0rad)
  Radius = 4
FEATURE [Part::Cylinder] Cylinder1955  label="Válec1955"
  Angle = 360
  AttacherType = Attacher::AttachEngine3D
  Height = 20
  Placement = pos=(25.4558,25.4558,0) rot=(0,0,1;0.785398rad)
  Radius = 1.5
FEATURE [Part::Cylinder] Cylinder1956  label="Válec1956"
  Angle = 360
  AttacherType = Attacher::AttachEngine3D
  Height = 20
  Placement = pos=(28,16,-3) rot=(0,1,0;1.5708rad)
  Radius = 1.5
FEATURE [Part::Cylinder] Cylinder1957  label="Válec1957"
  Angle = 360
  AttacherType = Attacher::AttachEngine3D
  Height = 30
  Placement = pos=(36,0,-24) rot=(0,0,1;0rad)
  Radius = 4
FEATURE [Part::Cylinder] Cylinder1958  label="Válec1958"
  Angle = 360
  AttacherType = Attacher::AttachEngine3D
  Height = 20
  Placement = pos=(26,37,7) rot=(0,1,0;1.5708rad)
  Radius = 1.5
FEATURE [Part::Cut] Cut518
  Base = -> Cut522
  Tool = -> Cylinder1958
FEATURE [Part::Box] Box451  label="Krychle451"
  AttacherType = Attacher::AttachEngine3D
  Height = 6
  Length = 2
  Placement = pos=(32,13,-6) rot=(0,0,1;0rad)
  Width = 6
FEATURE [Part::Cylinder] Cylinder1959  label="Válec1959"
  Angle = 360
  AttacherType = Attacher::AttachEngine3D
  Height = 12
  Placement = pos=(0,0,-6) rot=(0,0,1;0rad)
  Radius = 32
FEATURE [Part::Cut] Cut534
  Base = -> Box441
  Tool = -> Cylinder1959
FEATURE [Part::Cut] Cut520
  Base = -> Cut534
  Tool = -> Cylinder1957
FEATURE [Part::Cut] Cut531
  Base = -> Cut520
  Tool = -> Cylinder1948
FEATURE [Part::Cut] Cut540
  Base = -> Cut531
  Tool = -> Cylinder1950
FEATURE [Part::Cut] Cut527
  Base = -> Cut540
  Tool = -> Cylinder1942
FEATURE [Part::Cylinder] Cylinder1960  label="Válec1960"
  Angle = 360
  AttacherType = Attacher::AttachEngine3D
  Height = 6
  Placement = pos=(0,0,6) rot=(0,0,1;0rad)
  Radius = 40
FEATURE [Part::Cut] Cut521
  Base = -> Box448
  Tool = -> Cylinder1960
FEATURE [Part::Cylinder] Cylinder1961  label="Válec1961"
  Angle = 360
  AttacherType = Attacher::AttachEngine3D
  Height = 20
  Placement = pos=(36,0,0) rot=(0,0,1;0rad)
  Radius = 1.5
FEATURE [Part::Cylinder] Cylinder1962  label="Válec1962"
  Angle = 360
  AttacherType = Attacher::AttachEngine3D
  Height = 12
  Placement = pos=(0,0,-6) rot=(0,0,1;0rad)
  Radius = 32
FEATURE [Part::Cylinder] Cylinder1963  label="Válec1963"
  Angle = 360
  AttacherType = Attacher::AttachEngine3D
  Height = 20
  Placement = pos=(26,37,7) rot=(0,1,0;1.5708rad)
  Radius = 1.5
FEATURE [Part::Box] Box452  label="Krychle452"
  AttacherType = Attacher::AttachEngine3D
  Height = 6
  Length = 2
  Placement = pos=(30,34,4) rot=(0,0,1;0rad)
  Width = 6
FEATURE [Part::Cut] Cut512
  Base = -> Cut521
  Tool = -> Box452
FEATURE [Part::Cut] Cut526
  Base = -> Cut512
  Tool = -> Cylinder1953
FEATURE [Part::Cylinder] Cylinder1964  label="Válec1964"
  Angle = 360
  AttacherType = Attacher::AttachEngine3D
  Height = 30
  Placement = pos=(25.4558,25.4558,-24) rot=(0,0,1;0.785398rad)
  Radius = 4
FEATURE [Part::Box] Box453  label="Krychle453"
  AttacherType = Attacher::AttachEngine3D
  Height = 6
  Length = 2
  Placement = pos=(32,13,-6) rot=(0,0,1;0rad)
  Width = 6
FEATURE [Part::Cylinder] Cylinder1965  label="Válec1965"
  Angle = 360
  AttacherType = Attacher::AttachEngine3D
  Height = 12
  Placement = pos=(0,0,-6) rot=(0,0,1;0rad)
  Radius = 32
FEATURE [Part::Box] Box454  label="Krychle454"
  AttacherType = Attacher::AttachEngine3D
  Height = 6
  Length = 2
  Placement = pos=(30,34,4) rot=(0,0,1;0rad)
  Width = 6
FEATURE [Part::Cylinder] Cylinder1966  label="Válec1966"
  Angle = 360
  AttacherType = Attacher::AttachEngine3D
  Height = 20
  Placement = pos=(28,16,-3) rot=(0,1,0;1.5708rad)
  Radius = 1.5
FEATURE [Part::Cylinder] Cylinder1967  label="Válec1967"
  Angle = 360
  AttacherType = Attacher::AttachEngine3D
  Height = 12
  Placement = pos=(6,41.8,-6) rot=(0,0,1;0rad)
  Radius = 11
FEATURE [Part::Cut] Cut514
  Base = -> Box450
  Tool = -> Cylinder1967
FEATURE [Part::Cut] Cut525
  Base = -> Cut514
  Tool = -> Cylinder1965
FEATURE [Part::Cut] Cut535
  Base = -> Cut525
  Tool = -> Cylinder1939
FEATURE [Part::Cylinder] Cylinder1968  label="Válec1968"
  Angle = 360
  AttacherType = Attacher::AttachEngine3D
  Height = 20
  Placement = pos=(1.2e-14,-36,0) rot=(0,0,-1;1.5708rad)
  Radius = 1.5
FEATURE [Part::Box] Box455  label="Krychle455"
  AttacherType = Attacher::AttachEngine3D
  Height = 18
  Length = 14
  Placement = pos=(26,0,-6) rot=(0,0,1;0rad)
  Width = 40
FEATURE [Part::Cut] Cut533
  Base = -> Box455
  Tool = -> Cylinder1951
FEATURE [Part::Cut] Cut530
  Base = -> Cut533
  Tool = -> Cylinder1954
FEATURE [Part::Cut] Cut538
  Base = -> Cut530
  Tool = -> Cylinder1961
FEATURE [Part::Cut] Cut517
  Base = -> Cut538
  Tool = -> Cylinder1964
FEATURE [Part::Cut] Cut542
  Base = -> Cut517
  Tool = -> Cylinder1955
FEATURE [Part::Box] Box456  label="Krychle456"
  AttacherType = Attacher::AttachEngine3D
  Height = 12
  Length = 18
  Placement = pos=(8,10,-6) rot=(0,0,1;0rad)
  Width = 30
FEATURE [Part::Cylinder] Cylinder1969  label="Válec1969"
  Angle = 360
  AttacherType = Attacher::AttachEngine3D
  Height = 12
  Placement = pos=(6,41.8,-6) rot=(0,0,1;0rad)
  Radius = 11
FEATURE [Part::Cut] Cut529
  Base = -> Box456
  Tool = -> Cylinder1969
FEATURE [Part::Cut] Cut515
  Base = -> Cut529
  Tool = -> Cylinder1962
FEATURE [Part::Cylinder] Cylinder1970  label="Válec1970"
  Angle = 360
  AttacherType = Attacher::AttachEngine3D
  Height = 30
  Placement = pos=(25.4558,25.4558,-24) rot=(0,0,1;0.785398rad)
  Radius = 4
FEATURE [Part::Cut] Cut532
  Base = -> Cut515
  Tool = -> Cylinder1970
FEATURE [Part::Compound] Compound876
  Links = -> [Box443,Box442,Box437,Box447,Box445,Box446,Box449,Box440]
FEATURE [Part::Cut] Cut523
  Base = -> Tube085
  Tool = -> Compound876
FEATURE [Part::Compound] Compound878
  Links = -> [Cylinder1956,Cylinder1949]
FEATURE [Part::Cut] Cut536
  Base = -> Cut527
  Tool = -> Compound878
FEATURE [Part::Compound] Compound879
  Links = -> [Box451,Box444]
FEATURE [Part::Cut] Cut541
  Base = -> Cut536
  Tool = -> Compound879
FEATURE [Part::Compound] Compound880
  Links = -> [Cut541,Cut535,Cut518]
FEATURE [Part::Compound] Compound881
  Links = -> [Cylinder1966,Cylinder1963]
FEATURE [Part::Cut] Cut537
  Base = -> Cut542
  Tool = -> Compound881
FEATURE [Part::Compound] Compound882
  Links = -> [Cylinder1924,Cylinder1923,Cylinder1929,Cylinder1940,Cylinder1937,Cylinder1944,Cylinder1933,Cylinder1968]
FEATURE [Part::Cut] Cut539
  Base = -> Cut528
  Tool = -> Compound882
FEATURE [Part::Compound] Compound883
  Links = -> [Cylinder1941,Cylinder1945,Cylinder1943,Cylinder1936,Cylinder1952,Cylinder1946,Cylinder1938,Cylinder1935]
FEATURE [Part::Cut] Cut519
  Base = -> Cut523
  Tool = -> Compound883
FEATURE [Part::Compound] Compound884
  Links = -> [Box453,Box454]
FEATURE [Part::Cut] Cut524
  Base = -> Cut537
  Tool = -> Compound884
FEATURE [Part::Compound] Compound877
  Links = -> [Cut524,Cut532,Cut526]
FEATURE [Part::Mirroring] mirror002  label="Compound123 (mirrored)002"
  Base = (1,0,0)
  Normal = (1e-16,-1,0)
  Source = -> Compound877
FEATURE [Part::Compound] Compound875  label="J-mini_monoblock"
  Links = -> [Cut519,Compound880,mirror002,Cut539,Cut511]
FEATURE [Part::FeaturePython] Tube087  # WARN: FeaturePython — macro-defined, semantics opaque (R4)
  AttacherType = Attacher::AttachEngine3D
  Height = 13
  InnerRadius = 32.5
  OuterRadius = 40
  Placement = pos=(0,0,12) rot=(0,0,1;0rad)
FEATURE [Part::Box] Box474  label="Krychle474"
  AttacherType = Attacher::AttachEngine3D
  Height = 2
  Length = 9
  Placement = pos=(32,-3,14) rot=(0,0,1;0rad)
  Width = 6
FEATURE [Part::Box] Box475  label="Krychle475"
  AttacherType = Attacher::AttachEngine3D
  Height = 2
  Length = 9
  Placement = pos=(24.7487,20.5061,14) rot=(0,0,1;0.785398rad)
  Width = 6
FEATURE [Part::Box] Box477  label="Krychle477"
  AttacherType = Attacher::AttachEngine3D
  Height = 2
  Length = 9
  Placement = pos=(-20.5061,24.7487,14) rot=(0,0,1;2.35619rad)
  Width = 6
FEATURE [Part::Box] Box480  label="Krychle480"
  AttacherType = Attacher::AttachEngine3D
  Height = 2
  Length = 9
  Placement = pos=(-3,-32,14) rot=(0,0,-1;1.5708rad)
  Width = 6
FEATURE [Part::Box] Box476  label="Krychle476"
  AttacherType = Attacher::AttachEngine3D
  Height = 2
  Length = 9
  Placement = pos=(3,32,14) rot=(0,0,1;1.5708rad)
  Width = 6
FEATURE [Part::Box] Box481  label="Krychle481"
  AttacherType = Attacher::AttachEngine3D
  Height = 2
  Length = 9
  Placement = pos=(20.5061,-24.7487,14) rot=(0,0,-1;0.785398rad)
  Width = 6
FEATURE [Part::Box] Box479  label="Krychle479"
  AttacherType = Attacher::AttachEngine3D
  Height = 2
  Length = 9
  Placement = pos=(-24.7487,-20.5061,14) rot=(0,0,1;3.92699rad)
  Width = 6
FEATURE [Part::Box] Box478  label="Krychle478"
  AttacherType = Attacher::AttachEngine3D
  Height = 2
  Length = 9
  Placement = pos=(-32,3,14) rot=(0,0,1;3.14159rad)
  Width = 6
FEATURE [Part::Compound] Compound897
  Links = -> [Box474,Box475,Box476,Box477,Box478,Box479,Box480,Box481]
FEATURE [Part::Cylinder] Cylinder1996  label="Válec1996"
  Angle = 360
  AttacherType = Attacher::AttachEngine3D
  Height = 18
  Placement = pos=(-4e-15,36,0) rot=(0,0,1;1.5708rad)
  Radius = 1.5
FEATURE [Part::Cylinder] Cylinder1992  label="Válec1992"
  Angle = 360
  AttacherType = Attacher::AttachEngine3D
  Height = 18
  Placement = pos=(25.4558,25.4558,0) rot=(0,0,1;0.785398rad)
  Radius = 1.5
FEATURE [Part::Cylinder] Cylinder1993  label="Válec1993"
  Angle = 360
  AttacherType = Attacher::AttachEngine3D
  Height = 18
  Placement = pos=(25.4558,-25.4558,0) rot=(0,0,-1;0.785398rad)
  Radius = 1.5
FEATURE [Part::Cylinder] Cylinder1995  label="Válec1995"
  Angle = 360
  AttacherType = Attacher::AttachEngine3D
  Height = 18
  Placement = pos=(-25.4558,-25.4558,0) rot=(0,0,1;3.92699rad)
  Radius = 1.5
FEATURE [Part::Cylinder] Cylinder1990  label="Válec1990"
  Angle = 360
  AttacherType = Attacher::AttachEngine3D
  Height = 18
  Placement = pos=(-25.4558,25.4558,0) rot=(0,0,1;2.35619rad)
  Radius = 1.5
FEATURE [Part::Cylinder] Cylinder1994  label="Válec1994"
  Angle = 360
  AttacherType = Attacher::AttachEngine3D
  Height = 18
  Placement = pos=(1.2e-14,-36,0) rot=(0,0,-1;1.5708rad)
  Radius = 1.5
FEATURE [Part::Cylinder] Cylinder2003  label="Válec2003"
  Angle = 360
  AttacherType = Attacher::AttachEngine3D
  Height = 20
  Placement = pos=(26,37,19) rot=(0,1,0;1.5708rad)
  Radius = 1.5
FEATURE [Part::Box] Box486  label="Krychle486"
  AttacherType = Attacher::AttachEngine3D
  Height = 6
  Length = 2
  Placement = pos=(30,34,16) rot=(0,0,1;0rad)
  Width = 6
FEATURE [Part::Cylinder] Cylinder1991  label="Válec1991"
  Angle = 360
  AttacherType = Attacher::AttachEngine3D
  Height = 18
  Placement = pos=(-36,-1.1e-14,0) rot=(0,0,1;3.14159rad)
  Radius = 1.5
FEATURE [Part::Cylinder] Cylinder1998  label="Válec1998"
  Angle = 360
  AttacherType = Attacher::AttachEngine3D
  Height = 20
  Placement = pos=(26,37,19) rot=(0,1,0;1.5708rad)
  Radius = 1.5
FEATURE [Part::Box] Box485  label="Krychle485"
  AttacherType = Attacher::AttachEngine3D
  Height = 6
  Length = 2
  Placement = pos=(30,-40,16) rot=(0,0,1;0rad)
  Width = 6
FEATURE [Part::Cylinder] Cylinder1999  label="Válec1999"
  Angle = 360
  AttacherType = Attacher::AttachEngine3D
  Height = 20
  Placement = pos=(31,-21,22) rot=(0,1,0;1.5708rad)
  Radius = 1.5
FEATURE [Part::Cylinder] Cylinder1997  label="Válec1997"
  Angle = 360
  AttacherType = Attacher::AttachEngine3D
  Height = 10
  Placement = pos=(0,-32,20) rot=(0,0,1;0rad)
  Radius = 2.2
FEATURE [Part::Box] Box483  label="Krychle483"
  AttacherType = Attacher::AttachEngine3D
  Height = 6
  Length = 2
  Placement = pos=(34,-24,19) rot=(0,0,1;0rad)
  Width = 6
FEATURE [Part::Cylinder] Cylinder1989  label="Válec1989"
  Angle = 360
  AttacherType = Attacher::AttachEngine3D
  Height = 18
  Placement = pos=(36,0,0) rot=(0,0,1;0rad)
  Radius = 1.5
FEATURE [Part::Compound] Compound892
  Links = -> [Cylinder1992,Cylinder1996,Cylinder1990,Cylinder1991,Cylinder1995,Cylinder1994,Cylinder1993,Cylinder1989]
  Placement = pos=(0,0,4) rot=(0,0,1;0rad)
FEATURE [Part::Box] Box482  label="Krychle482"
  AttacherType = Attacher::AttachEngine3D
  Height = 6
  Length = 2
  Placement = pos=(30,34,16) rot=(0,0,1;0rad)
  Width = 6
FEATURE [Part::Cylinder] Cylinder2000  label="Válec2000"
  Angle = 360
  AttacherType = Attacher::AttachEngine3D
  Height = 20
  Placement = pos=(26,-37,19) rot=(0,1,0;1.5708rad)
  Radius = 1.5
FEATURE [Part::Box] Box484  label="Krychle484"
  AttacherType = Attacher::AttachEngine3D
  Height = 6
  Length = 2
  Placement = pos=(34,18,19) rot=(0,0,1;0rad)
  Width = 6
FEATURE [Part::Compound] Compound893
  Links = -> [Box482,Box484,Box485,Box483]
FEATURE [Part::Cylinder] Cylinder2001  label="Válec2001"
  Angle = 360
  AttacherType = Attacher::AttachEngine3D
  Height = 20
  Placement = pos=(31,21,22) rot=(0,1,0;1.5708rad)
  Radius = 1.5
FEATURE [Part::Compound] Compound894
  Links = -> [Cylinder1998,Cylinder2001,Cylinder1999,Cylinder2000]
FEATURE [Part::Cylinder] Cylinder2002  label="Válec2002"
  Angle = 360
  AttacherType = Attacher::AttachEngine3D
  Height = 20
  Placement = pos=(31,21,22) rot=(0,1,0;1.5708rad)
  Radius = 1.5
FEATURE [Part::Cylinder] Cylinder2004  label="Válec2004"
  Angle = 360
  AttacherType = Attacher::AttachEngine3D
  Height = 20
  Placement = pos=(31,-21,22) rot=(0,1,0;1.5708rad)
  Radius = 1.5
FEATURE [Part::Box] Box490  label="Krychle490"
  AttacherType = Attacher::AttachEngine3D
  Height = 13
  Length = 40
  Placement = pos=(0,-40,12) rot=(0,0,1;0rad)
  Width = 80
FEATURE [Part::Box] Box489  label="Krychle489"
  AttacherType = Attacher::AttachEngine3D
  Height = 6
  Length = 2
  Placement = pos=(34,18,19) rot=(0,0,1;0rad)
  Width = 6
FEATURE [Part::Cylinder] Cylinder2005  label="Válec2005"
  Angle = 360
  AttacherType = Attacher::AttachEngine3D
  Height = 13
  Placement = pos=(0,0,12) rot=(0,0,1;0rad)
  Radius = 40
FEATURE [Part::Cut] Cut558
  Base = -> Box490
  Tool = -> Cylinder2005
FEATURE [Part::Box] Box488  label="Krychle488"
  AttacherType = Attacher::AttachEngine3D
  Height = 6
  Length = 2
  Placement = pos=(34,-24,19) rot=(0,0,1;0rad)
  Width = 6
FEATURE [Part::Box] Box487  label="Krychle487"
  AttacherType = Attacher::AttachEngine3D
  Height = 6
  Length = 2
  Placement = pos=(30,-40,16) rot=(0,0,1;0rad)
  Width = 6
FEATURE [Part::Compound] Compound896
  Links = -> [Box486,Box489,Box487,Box488]
FEATURE [Part::Cut] Cut557
  Base = -> Cut558
  Tool = -> Compound896
FEATURE [Part::Cylinder] Cylinder2006  label="Válec2006"
  Angle = 360
  AttacherType = Attacher::AttachEngine3D
  Height = 20
  Placement = pos=(26,-37,19) rot=(0,1,0;1.5708rad)
  Radius = 1.5
FEATURE [Part::Compound] Compound895
  Links = -> [Cylinder2003,Cylinder2002,Cylinder2004,Cylinder2006]
FEATURE [Part::Cut] Cut559
  Base = -> Cut557
  Tool = -> Compound895
FEATURE [Part::Torus] Torus010  label="Anuloid010"
  Angle1 = -180
  Angle2 = 180
  Angle3 = 360
  AttacherType = Attacher::AttachEngine3D
  Placement = pos=(0,0,20) rot=(0,0,1;0rad)
  Radius1 = 31.75
  Radius2 = 2.2
FEATURE [Part::Cut] Cut552
  Base = -> Tube087
  Tool = -> Torus010
FEATURE [Part::Cut] Cut543
  Base = -> Cut552
  Tool = -> Compound897
FEATURE [Part::Cut] Cut553
  Base = -> Cut543
  Tool = -> Compound892
FEATURE [Part::Cut] Cut554
  Base = -> Cut553
  Tool = -> Cylinder1997
FEATURE [Part::Cut] Cut555
  Base = -> Cut554
  Tool = -> Compound893
FEATURE [Part::Cut] Cut556
  Base = -> Cut555
  Tool = -> Compound894
FEATURE [Part::Compound] Compound898  label="J-mini_bearing-ring-nuovo"
  Links = -> [Cut556,Cut559]
FEATURE [Mesh::Feature] Mesh  label="J-mini_bearing-ring-nuovo (Meshed)"
FEATURE [Mesh::Feature] Mesh008  label="J-mini_outer-gear (Meshed)001"
FEATURE [Mesh::Feature] Mesh009  label="J-mini_pikovina (Meshed)001"
FEATURE [Mesh::Feature] Mesh010  label="J-mini_inner-gear-high (Meshed)001"
FEATURE [Mesh::Feature] Mesh011  label="J-mini_rybovina-nuovo (Meshed)001"
FEATURE [Mesh::Feature] Mesh012  label="J-mini_pikovina-fixo (Meshed)001"
FEATURE [Mesh::Feature] Mesh013  label="J-mini_bearing-ring (Meshed)"
FEATURE [Mesh::Feature] Mesh014  label="J-mini_bearing-ring-nuovo (Meshed)001"
FEATURE [Mesh::Feature] Mesh015  label="J-mini_monoblock (Meshed)"
FEATURE [Mesh::Feature] Mesh016  label="J-mini_quikovina (Meshed)001"
FEATURE [Mesh::Feature] Mesh017  label="J-mini_inner-gear-high (Meshed)002"
FEATURE [Mesh::Feature] Mesh018  label="J-mini_inner-gear_low (Meshed)"
